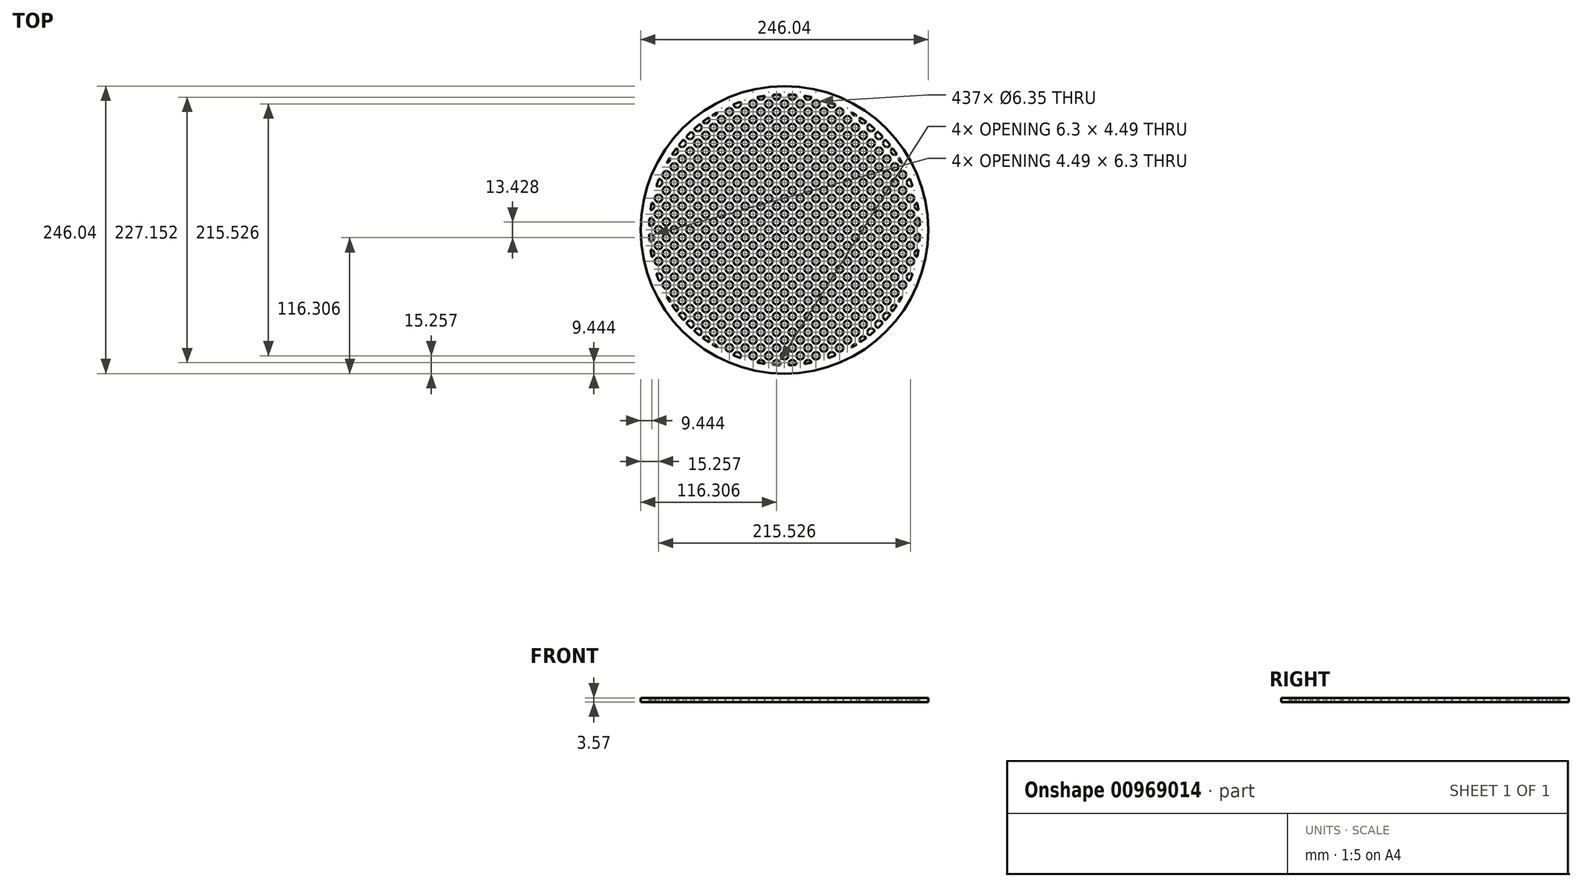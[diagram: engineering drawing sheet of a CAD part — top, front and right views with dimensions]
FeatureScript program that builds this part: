
annotation { "Feature Type Name" : "Feature", "Feature Type Description" : "" }
export const myFeature = defineFeature(function(context is Context, id is Id, definition is map)
    precondition{}
    {
        {
            var Q0;
            Q0=qCreatedBy(makeId("Top.planeOp"),FACE);
            var sketch = newSketch(context, id + "F0", { "sketchPlane" : qUnion([Q0])});
            skCircle(sketch, "E0", {"center": v(0, 0) * mm, "radius": 123.02 * mm});
            skSolve(sketch);
        }
        {
            var Q0;
            Q0 = qSketchRegion(id + "F0", true);
            extrude(context, id + "F1", {"entities" : qUnion([Q0]), "depth" : 3.57 * mm, "offsetDistance" : 25.4 * mm});
        }
        {
            var Q0;
            Q0=makeQuery(id+"F1.opExtrude","CAP_FACE",FACE,{"disambiguationData":[OSD([sQuery(id+"F0.wireOp",EDGE,"E0")])],"isStart":false});
            var sketch = newSketch(context, id + "F2", { "sketchPlane" : qUnion([Q0])});
            skCircle(sketch, "E1", {"center": v(-175.11, -121.23) * mm, "radius": 3.18 * mm});
            skCircle(sketch, "E2", {"center": v(-168.38, -114.5) * mm, "radius": 3.18 * mm});
            skLineSegment(sketch, "E3", {"start": v(-175.04, -116.82) * mm, "end": v(-170.43, -121.43) * mm, "construction": true});
            skLineSegment(sketch, "E4", {"start": v(-173.02, -114.35) * mm, "end": v(-167.94, -119.43) * mm, "construction": true});
            skLineSegment(sketch, "E5", {"start": v(-175.11, -121.23) * mm, "end": v(-168.38, -114.5) * mm, "construction": true});
            skCircle(sketch, "E6.0.1.0", {"center": v(-175.11, -107.76) * mm, "radius": 3.18 * mm});
            skCircle(sketch, "E6.0.2.0", {"center": v(-175.11, -94.3) * mm, "radius": 3.18 * mm});
            skCircle(sketch, "E6.1.0.0", {"center": v(-161.64, -121.23) * mm, "radius": 3.18 * mm});
            skCircle(sketch, "E6.1.1.0", {"center": v(-161.64, -107.76) * mm, "radius": 3.18 * mm});
            skCircle(sketch, "E6.1.2.0", {"center": v(-161.64, -94.3) * mm, "radius": 3.18 * mm});
            skCircle(sketch, "E6.2.0.0", {"center": v(-148.17, -121.23) * mm, "radius": 3.18 * mm});
            skCircle(sketch, "E6.2.1.0", {"center": v(-148.17, -107.76) * mm, "radius": 3.18 * mm});
            skCircle(sketch, "E6.2.2.0", {"center": v(-148.17, -94.3) * mm, "radius": 3.18 * mm});
            skLineSegment(sketch, "E6.direction1", {"start": v(-175.11, -121.23) * mm, "end": v(-161.64, -121.23) * mm, "construction": true});
            skLineSegment(sketch, "E6.direction2", {"start": v(-175.11, -121.23) * mm, "end": v(-175.11, -107.76) * mm, "construction": true});
            skCircle(sketch, "E7.0.1.0", {"center": v(-168.38, -101.03) * mm, "radius": 3.18 * mm});
            skCircle(sketch, "E7.0.2.0", {"center": v(-168.38, -87.56) * mm, "radius": 3.18 * mm});
            skCircle(sketch, "E7.1.0.0", {"center": v(-154.9, -114.5) * mm, "radius": 3.18 * mm});
            skCircle(sketch, "E7.1.1.0", {"center": v(-154.9, -101.03) * mm, "radius": 3.18 * mm});
            skCircle(sketch, "E7.1.2.0", {"center": v(-154.9, -87.56) * mm, "radius": 3.18 * mm});
            skCircle(sketch, "E7.2.0.0", {"center": v(-141.44, -114.5) * mm, "radius": 3.18 * mm});
            skCircle(sketch, "E7.2.1.0", {"center": v(-141.44, -101.03) * mm, "radius": 3.18 * mm});
            skCircle(sketch, "E7.2.2.0", {"center": v(-141.44, -87.56) * mm, "radius": 3.18 * mm});
            skLineSegment(sketch, "E7.direction1", {"start": v(-168.38, -114.5) * mm, "end": v(-154.9, -114.5) * mm, "construction": true});
            skLineSegment(sketch, "E7.direction2", {"start": v(-168.38, -114.5) * mm, "end": v(-168.38, -101.03) * mm, "construction": true});
            skCircle(sketch, "E8.0.0.3", {"center": v(-168.38, -74.09) * mm, "radius": 3.18 * mm});
            skCircle(sketch, "E8.0.0.4", {"center": v(-168.38, -60.62) * mm, "radius": 3.18 * mm});
            skCircle(sketch, "E8.0.0.5", {"center": v(-168.38, -47.15) * mm, "radius": 3.18 * mm});
            skCircle(sketch, "E8.0.0.6", {"center": v(-168.38, -33.68) * mm, "radius": 3.18 * mm});
            skCircle(sketch, "E8.0.0.7", {"center": v(-168.38, -20.2) * mm, "radius": 3.18 * mm});
            skCircle(sketch, "E8.0.0.8", {"center": v(-168.38, -6.74) * mm, "radius": 3.18 * mm});
            skCircle(sketch, "E8.0.0.9", {"center": v(-168.38, 6.74) * mm, "radius": 3.18 * mm});
            skCircle(sketch, "E8.0.0.10", {"center": v(-168.38, 20.2) * mm, "radius": 3.18 * mm});
            skCircle(sketch, "E8.0.0.11", {"center": v(-168.38, 33.68) * mm, "radius": 3.18 * mm});
            skCircle(sketch, "E8.0.0.12", {"center": v(-168.38, 47.15) * mm, "radius": 3.18 * mm});
            skCircle(sketch, "E8.0.0.13", {"center": v(-168.38, 60.62) * mm, "radius": 3.18 * mm});
            skCircle(sketch, "E8.0.0.14", {"center": v(-168.38, 74.09) * mm, "radius": 3.18 * mm});
            skCircle(sketch, "E8.0.0.15", {"center": v(-168.38, 87.56) * mm, "radius": 3.18 * mm});
            skCircle(sketch, "E8.0.0.16", {"center": v(-168.38, 101.03) * mm, "radius": 3.18 * mm});
            skCircle(sketch, "E8.0.0.17", {"center": v(-168.38, 114.5) * mm, "radius": 3.18 * mm});
            skCircle(sketch, "E8.0.0.18", {"center": v(-168.38, 127.97) * mm, "radius": 3.18 * mm});
            skCircle(sketch, "E8.0.0.19", {"center": v(-168.38, 141.44) * mm, "radius": 3.18 * mm});
            skCircle(sketch, "E8.0.0.20", {"center": v(-168.38, 154.9) * mm, "radius": 3.18 * mm});
            skCircle(sketch, "E8.0.0.21", {"center": v(-168.38, 168.38) * mm, "radius": 3.18 * mm});
            skCircle(sketch, "E8.0.0.22", {"center": v(-168.38, 181.85) * mm, "radius": 3.18 * mm});
            skCircle(sketch, "E8.0.0.23", {"center": v(-168.38, 195.32) * mm, "radius": 3.18 * mm});
            skCircle(sketch, "E8.0.0.24", {"center": v(-168.38, 208.8) * mm, "radius": 3.18 * mm});
            skCircle(sketch, "E8.0.1.3", {"center": v(-154.9, -74.09) * mm, "radius": 3.18 * mm});
            skCircle(sketch, "E8.0.1.4", {"center": v(-154.9, -60.62) * mm, "radius": 3.18 * mm});
            skCircle(sketch, "E8.0.1.5", {"center": v(-154.9, -47.15) * mm, "radius": 3.18 * mm});
            skCircle(sketch, "E8.0.1.6", {"center": v(-154.9, -33.68) * mm, "radius": 3.18 * mm});
            skCircle(sketch, "E8.0.1.7", {"center": v(-154.9, -20.2) * mm, "radius": 3.18 * mm});
            skCircle(sketch, "E8.0.1.8", {"center": v(-154.9, -6.74) * mm, "radius": 3.18 * mm});
            skCircle(sketch, "E8.0.1.9", {"center": v(-154.9, 6.74) * mm, "radius": 3.18 * mm});
            skCircle(sketch, "E8.0.1.10", {"center": v(-154.9, 20.2) * mm, "radius": 3.18 * mm});
            skCircle(sketch, "E8.0.1.11", {"center": v(-154.9, 33.68) * mm, "radius": 3.18 * mm});
            skCircle(sketch, "E8.0.1.12", {"center": v(-154.9, 47.15) * mm, "radius": 3.18 * mm});
            skCircle(sketch, "E8.0.1.13", {"center": v(-154.9, 60.62) * mm, "radius": 3.18 * mm});
            skCircle(sketch, "E8.0.1.14", {"center": v(-154.9, 74.09) * mm, "radius": 3.18 * mm});
            skCircle(sketch, "E8.0.1.15", {"center": v(-154.9, 87.56) * mm, "radius": 3.18 * mm});
            skCircle(sketch, "E8.0.1.16", {"center": v(-154.9, 101.03) * mm, "radius": 3.18 * mm});
            skCircle(sketch, "E8.0.1.17", {"center": v(-154.9, 114.5) * mm, "radius": 3.18 * mm});
            skCircle(sketch, "E8.0.1.18", {"center": v(-154.9, 127.97) * mm, "radius": 3.18 * mm});
            skCircle(sketch, "E8.0.1.19", {"center": v(-154.9, 141.44) * mm, "radius": 3.18 * mm});
            skCircle(sketch, "E8.0.1.20", {"center": v(-154.9, 154.9) * mm, "radius": 3.18 * mm});
            skCircle(sketch, "E8.0.1.21", {"center": v(-154.9, 168.38) * mm, "radius": 3.18 * mm});
            skCircle(sketch, "E8.0.1.22", {"center": v(-154.9, 181.85) * mm, "radius": 3.18 * mm});
            skCircle(sketch, "E8.0.1.23", {"center": v(-154.9, 195.32) * mm, "radius": 3.18 * mm});
            skCircle(sketch, "E8.0.1.24", {"center": v(-154.9, 208.8) * mm, "radius": 3.18 * mm});
            skCircle(sketch, "E8.0.2.3", {"center": v(-141.44, -74.09) * mm, "radius": 3.18 * mm});
            skCircle(sketch, "E8.0.2.4", {"center": v(-141.44, -60.62) * mm, "radius": 3.18 * mm});
            skCircle(sketch, "E8.0.2.5", {"center": v(-141.44, -47.15) * mm, "radius": 3.18 * mm});
            skCircle(sketch, "E8.0.2.6", {"center": v(-141.44, -33.68) * mm, "radius": 3.18 * mm});
            skCircle(sketch, "E8.0.2.7", {"center": v(-141.44, -20.2) * mm, "radius": 3.18 * mm});
            skCircle(sketch, "E8.0.2.8", {"center": v(-141.44, -6.74) * mm, "radius": 3.18 * mm});
            skCircle(sketch, "E8.0.2.9", {"center": v(-141.44, 6.74) * mm, "radius": 3.18 * mm});
            skCircle(sketch, "E8.0.2.10", {"center": v(-141.44, 20.2) * mm, "radius": 3.18 * mm});
            skCircle(sketch, "E8.0.2.11", {"center": v(-141.44, 33.68) * mm, "radius": 3.18 * mm});
            skCircle(sketch, "E8.0.2.12", {"center": v(-141.44, 47.15) * mm, "radius": 3.18 * mm});
            skCircle(sketch, "E8.0.2.13", {"center": v(-141.44, 60.62) * mm, "radius": 3.18 * mm});
            skCircle(sketch, "E8.0.2.14", {"center": v(-141.44, 74.09) * mm, "radius": 3.18 * mm});
            skCircle(sketch, "E8.0.2.15", {"center": v(-141.44, 87.56) * mm, "radius": 3.18 * mm});
            skCircle(sketch, "E8.0.2.16", {"center": v(-141.44, 101.03) * mm, "radius": 3.18 * mm});
            skCircle(sketch, "E8.0.2.17", {"center": v(-141.44, 114.5) * mm, "radius": 3.18 * mm});
            skCircle(sketch, "E8.0.2.18", {"center": v(-141.44, 127.97) * mm, "radius": 3.18 * mm});
            skCircle(sketch, "E8.0.2.19", {"center": v(-141.44, 141.44) * mm, "radius": 3.18 * mm});
            skCircle(sketch, "E8.0.2.20", {"center": v(-141.44, 154.9) * mm, "radius": 3.18 * mm});
            skCircle(sketch, "E8.0.2.21", {"center": v(-141.44, 168.38) * mm, "radius": 3.18 * mm});
            skCircle(sketch, "E8.0.2.22", {"center": v(-141.44, 181.85) * mm, "radius": 3.18 * mm});
            skCircle(sketch, "E8.0.2.23", {"center": v(-141.44, 195.32) * mm, "radius": 3.18 * mm});
            skCircle(sketch, "E8.0.2.24", {"center": v(-141.44, 208.8) * mm, "radius": 3.18 * mm});
            skCircle(sketch, "E9.0.0.3", {"center": v(-175.11, -80.82) * mm, "radius": 3.18 * mm});
            skCircle(sketch, "E9.0.0.4", {"center": v(-175.11, -67.35) * mm, "radius": 3.18 * mm});
            skCircle(sketch, "E9.0.0.5", {"center": v(-175.11, -53.88) * mm, "radius": 3.18 * mm});
            skCircle(sketch, "E9.0.0.6", {"center": v(-175.11, -40.41) * mm, "radius": 3.18 * mm});
            skCircle(sketch, "E9.0.0.7", {"center": v(-175.11, -26.94) * mm, "radius": 3.18 * mm});
            skCircle(sketch, "E9.0.0.8", {"center": v(-175.11, -13.47) * mm, "radius": 3.18 * mm});
            skCircle(sketch, "E9.0.0.9", {"center": v(-175.11, 0) * mm, "radius": 3.18 * mm});
            skCircle(sketch, "E9.0.0.10", {"center": v(-175.11, 13.47) * mm, "radius": 3.18 * mm});
            skCircle(sketch, "E9.0.0.11", {"center": v(-175.11, 26.94) * mm, "radius": 3.18 * mm});
            skCircle(sketch, "E9.0.0.12", {"center": v(-175.11, 40.41) * mm, "radius": 3.18 * mm});
            skCircle(sketch, "E9.0.0.13", {"center": v(-175.11, 53.88) * mm, "radius": 3.18 * mm});
            skCircle(sketch, "E9.0.0.14", {"center": v(-175.11, 67.35) * mm, "radius": 3.18 * mm});
            skCircle(sketch, "E9.0.0.15", {"center": v(-175.11, 80.82) * mm, "radius": 3.18 * mm});
            skCircle(sketch, "E9.0.0.16", {"center": v(-175.11, 94.3) * mm, "radius": 3.18 * mm});
            skCircle(sketch, "E9.0.0.17", {"center": v(-175.11, 107.76) * mm, "radius": 3.18 * mm});
            skCircle(sketch, "E9.0.0.18", {"center": v(-175.11, 121.23) * mm, "radius": 3.18 * mm});
            skCircle(sketch, "E9.0.0.19", {"center": v(-175.11, 134.7) * mm, "radius": 3.18 * mm});
            skCircle(sketch, "E9.0.0.20", {"center": v(-175.11, 148.17) * mm, "radius": 3.18 * mm});
            skCircle(sketch, "E9.0.0.21", {"center": v(-175.11, 161.64) * mm, "radius": 3.18 * mm});
            skCircle(sketch, "E9.0.0.22", {"center": v(-175.11, 175.11) * mm, "radius": 3.18 * mm});
            skCircle(sketch, "E9.0.0.23", {"center": v(-175.11, 188.59) * mm, "radius": 3.18 * mm});
            skCircle(sketch, "E9.0.0.24", {"center": v(-175.11, 202.06) * mm, "radius": 3.18 * mm});
            skCircle(sketch, "E9.0.1.3", {"center": v(-161.64, -80.82) * mm, "radius": 3.18 * mm});
            skCircle(sketch, "E9.0.1.4", {"center": v(-161.64, -67.35) * mm, "radius": 3.18 * mm});
            skCircle(sketch, "E9.0.1.5", {"center": v(-161.64, -53.88) * mm, "radius": 3.18 * mm});
            skCircle(sketch, "E9.0.1.6", {"center": v(-161.64, -40.41) * mm, "radius": 3.18 * mm});
            skCircle(sketch, "E9.0.1.7", {"center": v(-161.64, -26.94) * mm, "radius": 3.18 * mm});
            skCircle(sketch, "E9.0.1.8", {"center": v(-161.64, -13.47) * mm, "radius": 3.18 * mm});
            skCircle(sketch, "E9.0.1.9", {"center": v(-161.64, 0) * mm, "radius": 3.18 * mm});
            skCircle(sketch, "E9.0.1.10", {"center": v(-161.64, 13.47) * mm, "radius": 3.18 * mm});
            skCircle(sketch, "E9.0.1.11", {"center": v(-161.64, 26.94) * mm, "radius": 3.18 * mm});
            skCircle(sketch, "E9.0.1.12", {"center": v(-161.64, 40.41) * mm, "radius": 3.18 * mm});
            skCircle(sketch, "E9.0.1.13", {"center": v(-161.64, 53.88) * mm, "radius": 3.18 * mm});
            skCircle(sketch, "E9.0.1.14", {"center": v(-161.64, 67.35) * mm, "radius": 3.18 * mm});
            skCircle(sketch, "E9.0.1.15", {"center": v(-161.64, 80.82) * mm, "radius": 3.18 * mm});
            skCircle(sketch, "E9.0.1.16", {"center": v(-161.64, 94.3) * mm, "radius": 3.18 * mm});
            skCircle(sketch, "E9.0.1.17", {"center": v(-161.64, 107.76) * mm, "radius": 3.18 * mm});
            skCircle(sketch, "E9.0.1.18", {"center": v(-161.64, 121.23) * mm, "radius": 3.18 * mm});
            skCircle(sketch, "E9.0.1.19", {"center": v(-161.64, 134.7) * mm, "radius": 3.18 * mm});
            skCircle(sketch, "E9.0.1.20", {"center": v(-161.64, 148.17) * mm, "radius": 3.18 * mm});
            skCircle(sketch, "E9.0.1.21", {"center": v(-161.64, 161.64) * mm, "radius": 3.18 * mm});
            skCircle(sketch, "E9.0.1.22", {"center": v(-161.64, 175.11) * mm, "radius": 3.18 * mm});
            skCircle(sketch, "E9.0.1.23", {"center": v(-161.64, 188.59) * mm, "radius": 3.18 * mm});
            skCircle(sketch, "E9.0.1.24", {"center": v(-161.64, 202.06) * mm, "radius": 3.18 * mm});
            skCircle(sketch, "E9.0.2.3", {"center": v(-148.17, -80.82) * mm, "radius": 3.18 * mm});
            skCircle(sketch, "E9.0.2.4", {"center": v(-148.17, -67.35) * mm, "radius": 3.18 * mm});
            skCircle(sketch, "E9.0.2.5", {"center": v(-148.17, -53.88) * mm, "radius": 3.18 * mm});
            skCircle(sketch, "E9.0.2.6", {"center": v(-148.17, -40.41) * mm, "radius": 3.18 * mm});
            skCircle(sketch, "E9.0.2.7", {"center": v(-148.17, -26.94) * mm, "radius": 3.18 * mm});
            skCircle(sketch, "E9.0.2.8", {"center": v(-148.17, -13.47) * mm, "radius": 3.18 * mm});
            skCircle(sketch, "E9.0.2.9", {"center": v(-148.17, 0) * mm, "radius": 3.18 * mm});
            skCircle(sketch, "E9.0.2.10", {"center": v(-148.17, 13.47) * mm, "radius": 3.18 * mm});
            skCircle(sketch, "E9.0.2.11", {"center": v(-148.17, 26.94) * mm, "radius": 3.18 * mm});
            skCircle(sketch, "E9.0.2.12", {"center": v(-148.17, 40.41) * mm, "radius": 3.18 * mm});
            skCircle(sketch, "E9.0.2.13", {"center": v(-148.17, 53.88) * mm, "radius": 3.18 * mm});
            skCircle(sketch, "E9.0.2.14", {"center": v(-148.17, 67.35) * mm, "radius": 3.18 * mm});
            skCircle(sketch, "E9.0.2.15", {"center": v(-148.17, 80.82) * mm, "radius": 3.18 * mm});
            skCircle(sketch, "E9.0.2.16", {"center": v(-148.17, 94.3) * mm, "radius": 3.18 * mm});
            skCircle(sketch, "E9.0.2.17", {"center": v(-148.17, 107.76) * mm, "radius": 3.18 * mm});
            skCircle(sketch, "E9.0.2.18", {"center": v(-148.17, 121.23) * mm, "radius": 3.18 * mm});
            skCircle(sketch, "E9.0.2.19", {"center": v(-148.17, 134.7) * mm, "radius": 3.18 * mm});
            skCircle(sketch, "E9.0.2.20", {"center": v(-148.17, 148.17) * mm, "radius": 3.18 * mm});
            skCircle(sketch, "E9.0.2.21", {"center": v(-148.17, 161.64) * mm, "radius": 3.18 * mm});
            skCircle(sketch, "E9.0.2.22", {"center": v(-148.17, 175.11) * mm, "radius": 3.18 * mm});
            skCircle(sketch, "E9.0.2.23", {"center": v(-148.17, 188.59) * mm, "radius": 3.18 * mm});
            skCircle(sketch, "E9.0.2.24", {"center": v(-148.17, 202.06) * mm, "radius": 3.18 * mm});
            skCircle(sketch, "E10.0.3.0", {"center": v(-134.7, -121.23) * mm, "radius": 3.18 * mm});
            skCircle(sketch, "E10.0.3.1", {"center": v(-134.7, -107.76) * mm, "radius": 3.18 * mm});
            skCircle(sketch, "E10.0.3.2", {"center": v(-134.7, -94.3) * mm, "radius": 3.18 * mm});
            skCircle(sketch, "E10.0.3.3", {"center": v(-134.7, -80.82) * mm, "radius": 3.18 * mm});
            skCircle(sketch, "E10.0.3.4", {"center": v(-134.7, -67.35) * mm, "radius": 3.18 * mm});
            skCircle(sketch, "E10.0.3.5", {"center": v(-134.7, -53.88) * mm, "radius": 3.18 * mm});
            skCircle(sketch, "E10.0.3.6", {"center": v(-134.7, -40.41) * mm, "radius": 3.18 * mm});
            skCircle(sketch, "E10.0.3.7", {"center": v(-134.7, -26.94) * mm, "radius": 3.18 * mm});
            skCircle(sketch, "E10.0.3.8", {"center": v(-134.7, -13.47) * mm, "radius": 3.18 * mm});
            skCircle(sketch, "E10.0.3.9", {"center": v(-134.7, 0) * mm, "radius": 3.18 * mm});
            skCircle(sketch, "E10.0.3.10", {"center": v(-134.7, 13.47) * mm, "radius": 3.18 * mm});
            skCircle(sketch, "E10.0.3.11", {"center": v(-134.7, 26.94) * mm, "radius": 3.18 * mm});
            skCircle(sketch, "E10.0.3.12", {"center": v(-134.7, 40.41) * mm, "radius": 3.18 * mm});
            skCircle(sketch, "E10.0.3.13", {"center": v(-134.7, 53.88) * mm, "radius": 3.18 * mm});
            skCircle(sketch, "E10.0.3.14", {"center": v(-134.7, 67.35) * mm, "radius": 3.18 * mm});
            skCircle(sketch, "E10.0.3.15", {"center": v(-134.7, 80.82) * mm, "radius": 3.18 * mm});
            skCircle(sketch, "E10.0.3.16", {"center": v(-134.7, 94.3) * mm, "radius": 3.18 * mm});
            skCircle(sketch, "E10.0.3.17", {"center": v(-134.7, 107.76) * mm, "radius": 3.18 * mm});
            skCircle(sketch, "E10.0.3.18", {"center": v(-134.7, 121.23) * mm, "radius": 3.18 * mm});
            skCircle(sketch, "E10.0.3.19", {"center": v(-134.7, 134.7) * mm, "radius": 3.18 * mm});
            skCircle(sketch, "E10.0.3.20", {"center": v(-134.7, 148.17) * mm, "radius": 3.18 * mm});
            skCircle(sketch, "E10.0.3.21", {"center": v(-134.7, 161.64) * mm, "radius": 3.18 * mm});
            skCircle(sketch, "E10.0.3.22", {"center": v(-134.7, 175.11) * mm, "radius": 3.18 * mm});
            skCircle(sketch, "E10.0.3.23", {"center": v(-134.7, 188.59) * mm, "radius": 3.18 * mm});
            skCircle(sketch, "E10.0.3.24", {"center": v(-134.7, 202.06) * mm, "radius": 3.18 * mm});
            skCircle(sketch, "E10.0.4.0", {"center": v(-121.23, -121.23) * mm, "radius": 3.18 * mm});
            skCircle(sketch, "E10.0.4.1", {"center": v(-121.23, -107.76) * mm, "radius": 3.18 * mm});
            skCircle(sketch, "E10.0.4.2", {"center": v(-121.23, -94.3) * mm, "radius": 3.18 * mm});
            skCircle(sketch, "E10.0.4.3", {"center": v(-121.23, -80.82) * mm, "radius": 3.18 * mm});
            skCircle(sketch, "E10.0.4.4", {"center": v(-121.23, -67.35) * mm, "radius": 3.18 * mm});
            skCircle(sketch, "E10.0.4.5", {"center": v(-121.23, -53.88) * mm, "radius": 3.18 * mm});
            skCircle(sketch, "E10.0.4.6", {"center": v(-121.23, -40.41) * mm, "radius": 3.18 * mm});
            skCircle(sketch, "E10.0.4.7", {"center": v(-121.23, -26.94) * mm, "radius": 3.18 * mm});
            skCircle(sketch, "E10.0.4.8", {"center": v(-121.23, -13.47) * mm, "radius": 3.18 * mm});
            skCircle(sketch, "E10.0.4.9", {"center": v(-121.23, 0) * mm, "radius": 3.18 * mm});
            skCircle(sketch, "E10.0.4.10", {"center": v(-121.23, 13.47) * mm, "radius": 3.18 * mm});
            skCircle(sketch, "E10.0.4.11", {"center": v(-121.23, 26.94) * mm, "radius": 3.18 * mm});
            skCircle(sketch, "E10.0.4.12", {"center": v(-121.23, 40.41) * mm, "radius": 3.18 * mm});
            skCircle(sketch, "E10.0.4.13", {"center": v(-121.23, 53.88) * mm, "radius": 3.18 * mm});
            skCircle(sketch, "E10.0.4.14", {"center": v(-121.23, 67.35) * mm, "radius": 3.18 * mm});
            skCircle(sketch, "E10.0.4.15", {"center": v(-121.23, 80.82) * mm, "radius": 3.18 * mm});
            skCircle(sketch, "E10.0.4.16", {"center": v(-121.23, 94.3) * mm, "radius": 3.18 * mm});
            skCircle(sketch, "E10.0.4.17", {"center": v(-121.23, 107.76) * mm, "radius": 3.18 * mm});
            skCircle(sketch, "E10.0.4.18", {"center": v(-121.23, 121.23) * mm, "radius": 3.18 * mm});
            skCircle(sketch, "E10.0.4.19", {"center": v(-121.23, 134.7) * mm, "radius": 3.18 * mm});
            skCircle(sketch, "E10.0.4.20", {"center": v(-121.23, 148.17) * mm, "radius": 3.18 * mm});
            skCircle(sketch, "E10.0.4.21", {"center": v(-121.23, 161.64) * mm, "radius": 3.18 * mm});
            skCircle(sketch, "E10.0.4.22", {"center": v(-121.23, 175.11) * mm, "radius": 3.18 * mm});
            skCircle(sketch, "E10.0.4.23", {"center": v(-121.23, 188.59) * mm, "radius": 3.18 * mm});
            skCircle(sketch, "E10.0.4.24", {"center": v(-121.23, 202.06) * mm, "radius": 3.18 * mm});
            skCircle(sketch, "E10.0.5.0", {"center": v(-107.76, -121.23) * mm, "radius": 3.18 * mm});
            skCircle(sketch, "E10.0.5.1", {"center": v(-107.76, -107.76) * mm, "radius": 3.18 * mm});
            skCircle(sketch, "E10.0.5.2", {"center": v(-107.76, -94.3) * mm, "radius": 3.18 * mm});
            skCircle(sketch, "E10.0.5.3", {"center": v(-107.76, -80.82) * mm, "radius": 3.18 * mm});
            skCircle(sketch, "E10.0.5.4", {"center": v(-107.76, -67.35) * mm, "radius": 3.18 * mm});
            skCircle(sketch, "E10.0.5.5", {"center": v(-107.76, -53.88) * mm, "radius": 3.18 * mm});
            skCircle(sketch, "E10.0.5.6", {"center": v(-107.76, -40.41) * mm, "radius": 3.18 * mm});
            skCircle(sketch, "E10.0.5.7", {"center": v(-107.76, -26.94) * mm, "radius": 3.18 * mm});
            skCircle(sketch, "E10.0.5.8", {"center": v(-107.76, -13.47) * mm, "radius": 3.18 * mm});
            skCircle(sketch, "E10.0.5.9", {"center": v(-107.76, 0) * mm, "radius": 3.18 * mm});
            skCircle(sketch, "E10.0.5.10", {"center": v(-107.76, 13.47) * mm, "radius": 3.18 * mm});
            skCircle(sketch, "E10.0.5.11", {"center": v(-107.76, 26.94) * mm, "radius": 3.18 * mm});
            skCircle(sketch, "E10.0.5.12", {"center": v(-107.76, 40.41) * mm, "radius": 3.18 * mm});
            skCircle(sketch, "E10.0.5.13", {"center": v(-107.76, 53.88) * mm, "radius": 3.18 * mm});
            skCircle(sketch, "E10.0.5.14", {"center": v(-107.76, 67.35) * mm, "radius": 3.18 * mm});
            skCircle(sketch, "E10.0.5.15", {"center": v(-107.76, 80.82) * mm, "radius": 3.18 * mm});
            skCircle(sketch, "E10.0.5.16", {"center": v(-107.76, 94.3) * mm, "radius": 3.18 * mm});
            skCircle(sketch, "E10.0.5.17", {"center": v(-107.76, 107.76) * mm, "radius": 3.18 * mm});
            skCircle(sketch, "E10.0.5.18", {"center": v(-107.76, 121.23) * mm, "radius": 3.18 * mm});
            skCircle(sketch, "E10.0.5.19", {"center": v(-107.76, 134.7) * mm, "radius": 3.18 * mm});
            skCircle(sketch, "E10.0.5.20", {"center": v(-107.76, 148.17) * mm, "radius": 3.18 * mm});
            skCircle(sketch, "E10.0.5.21", {"center": v(-107.76, 161.64) * mm, "radius": 3.18 * mm});
            skCircle(sketch, "E10.0.5.22", {"center": v(-107.76, 175.11) * mm, "radius": 3.18 * mm});
            skCircle(sketch, "E10.0.5.23", {"center": v(-107.76, 188.59) * mm, "radius": 3.18 * mm});
            skCircle(sketch, "E10.0.5.24", {"center": v(-107.76, 202.06) * mm, "radius": 3.18 * mm});
            skCircle(sketch, "E10.0.6.0", {"center": v(-94.3, -121.23) * mm, "radius": 3.18 * mm});
            skCircle(sketch, "E10.0.6.1", {"center": v(-94.3, -107.76) * mm, "radius": 3.18 * mm});
            skCircle(sketch, "E10.0.6.2", {"center": v(-94.3, -94.3) * mm, "radius": 3.18 * mm});
            skCircle(sketch, "E10.0.6.3", {"center": v(-94.3, -80.82) * mm, "radius": 3.18 * mm});
            skCircle(sketch, "E10.0.6.4", {"center": v(-94.3, -67.35) * mm, "radius": 3.18 * mm});
            skCircle(sketch, "E10.0.6.5", {"center": v(-94.3, -53.88) * mm, "radius": 3.18 * mm});
            skCircle(sketch, "E10.0.6.6", {"center": v(-94.3, -40.41) * mm, "radius": 3.18 * mm});
            skCircle(sketch, "E10.0.6.7", {"center": v(-94.3, -26.94) * mm, "radius": 3.18 * mm});
            skCircle(sketch, "E10.0.6.8", {"center": v(-94.3, -13.47) * mm, "radius": 3.18 * mm});
            skCircle(sketch, "E10.0.6.9", {"center": v(-94.3, 0) * mm, "radius": 3.18 * mm});
            skCircle(sketch, "E10.0.6.10", {"center": v(-94.3, 13.47) * mm, "radius": 3.18 * mm});
            skCircle(sketch, "E10.0.6.11", {"center": v(-94.3, 26.94) * mm, "radius": 3.18 * mm});
            skCircle(sketch, "E10.0.6.12", {"center": v(-94.3, 40.41) * mm, "radius": 3.18 * mm});
            skCircle(sketch, "E10.0.6.13", {"center": v(-94.3, 53.88) * mm, "radius": 3.18 * mm});
            skCircle(sketch, "E10.0.6.14", {"center": v(-94.3, 67.35) * mm, "radius": 3.18 * mm});
            skCircle(sketch, "E10.0.6.15", {"center": v(-94.3, 80.82) * mm, "radius": 3.18 * mm});
            skCircle(sketch, "E10.0.6.16", {"center": v(-94.3, 94.3) * mm, "radius": 3.18 * mm});
            skCircle(sketch, "E10.0.6.17", {"center": v(-94.3, 107.76) * mm, "radius": 3.18 * mm});
            skCircle(sketch, "E10.0.6.18", {"center": v(-94.3, 121.23) * mm, "radius": 3.18 * mm});
            skCircle(sketch, "E10.0.6.19", {"center": v(-94.3, 134.7) * mm, "radius": 3.18 * mm});
            skCircle(sketch, "E10.0.6.20", {"center": v(-94.3, 148.17) * mm, "radius": 3.18 * mm});
            skCircle(sketch, "E10.0.6.21", {"center": v(-94.3, 161.64) * mm, "radius": 3.18 * mm});
            skCircle(sketch, "E10.0.6.22", {"center": v(-94.3, 175.11) * mm, "radius": 3.18 * mm});
            skCircle(sketch, "E10.0.6.23", {"center": v(-94.3, 188.59) * mm, "radius": 3.18 * mm});
            skCircle(sketch, "E10.0.6.24", {"center": v(-94.3, 202.06) * mm, "radius": 3.18 * mm});
            skCircle(sketch, "E10.0.7.0", {"center": v(-80.82, -121.23) * mm, "radius": 3.18 * mm});
            skCircle(sketch, "E10.0.7.1", {"center": v(-80.82, -107.76) * mm, "radius": 3.18 * mm});
            skCircle(sketch, "E10.0.7.2", {"center": v(-80.82, -94.3) * mm, "radius": 3.18 * mm});
            skCircle(sketch, "E10.0.7.3", {"center": v(-80.82, -80.82) * mm, "radius": 3.18 * mm});
            skCircle(sketch, "E10.0.7.4", {"center": v(-80.82, -67.35) * mm, "radius": 3.18 * mm});
            skCircle(sketch, "E10.0.7.5", {"center": v(-80.82, -53.88) * mm, "radius": 3.18 * mm});
            skCircle(sketch, "E10.0.7.6", {"center": v(-80.82, -40.41) * mm, "radius": 3.18 * mm});
            skCircle(sketch, "E10.0.7.7", {"center": v(-80.82, -26.94) * mm, "radius": 3.18 * mm});
            skCircle(sketch, "E10.0.7.8", {"center": v(-80.82, -13.47) * mm, "radius": 3.18 * mm});
            skCircle(sketch, "E10.0.7.9", {"center": v(-80.82, 0) * mm, "radius": 3.18 * mm});
            skCircle(sketch, "E10.0.7.10", {"center": v(-80.82, 13.47) * mm, "radius": 3.18 * mm});
            skCircle(sketch, "E10.0.7.11", {"center": v(-80.82, 26.94) * mm, "radius": 3.18 * mm});
            skCircle(sketch, "E10.0.7.12", {"center": v(-80.82, 40.41) * mm, "radius": 3.18 * mm});
            skCircle(sketch, "E10.0.7.13", {"center": v(-80.82, 53.88) * mm, "radius": 3.18 * mm});
            skCircle(sketch, "E10.0.7.14", {"center": v(-80.82, 67.35) * mm, "radius": 3.18 * mm});
            skCircle(sketch, "E10.0.7.15", {"center": v(-80.82, 80.82) * mm, "radius": 3.18 * mm});
            skCircle(sketch, "E10.0.7.16", {"center": v(-80.82, 94.3) * mm, "radius": 3.18 * mm});
            skCircle(sketch, "E10.0.7.17", {"center": v(-80.82, 107.76) * mm, "radius": 3.18 * mm});
            skCircle(sketch, "E10.0.7.18", {"center": v(-80.82, 121.23) * mm, "radius": 3.18 * mm});
            skCircle(sketch, "E10.0.7.19", {"center": v(-80.82, 134.7) * mm, "radius": 3.18 * mm});
            skCircle(sketch, "E10.0.7.20", {"center": v(-80.82, 148.17) * mm, "radius": 3.18 * mm});
            skCircle(sketch, "E10.0.7.21", {"center": v(-80.82, 161.64) * mm, "radius": 3.18 * mm});
            skCircle(sketch, "E10.0.7.22", {"center": v(-80.82, 175.11) * mm, "radius": 3.18 * mm});
            skCircle(sketch, "E10.0.7.23", {"center": v(-80.82, 188.59) * mm, "radius": 3.18 * mm});
            skCircle(sketch, "E10.0.7.24", {"center": v(-80.82, 202.06) * mm, "radius": 3.18 * mm});
            skCircle(sketch, "E10.0.8.0", {"center": v(-67.35, -121.23) * mm, "radius": 3.18 * mm});
            skCircle(sketch, "E10.0.8.1", {"center": v(-67.35, -107.76) * mm, "radius": 3.18 * mm});
            skCircle(sketch, "E10.0.8.2", {"center": v(-67.35, -94.3) * mm, "radius": 3.18 * mm});
            skCircle(sketch, "E10.0.8.3", {"center": v(-67.35, -80.82) * mm, "radius": 3.18 * mm});
            skCircle(sketch, "E10.0.8.4", {"center": v(-67.35, -67.35) * mm, "radius": 3.18 * mm});
            skCircle(sketch, "E10.0.8.5", {"center": v(-67.35, -53.88) * mm, "radius": 3.18 * mm});
            skCircle(sketch, "E10.0.8.6", {"center": v(-67.35, -40.41) * mm, "radius": 3.18 * mm});
            skCircle(sketch, "E10.0.8.7", {"center": v(-67.35, -26.94) * mm, "radius": 3.18 * mm});
            skCircle(sketch, "E10.0.8.8", {"center": v(-67.35, -13.47) * mm, "radius": 3.18 * mm});
            skCircle(sketch, "E10.0.8.9", {"center": v(-67.35, 0) * mm, "radius": 3.18 * mm});
            skCircle(sketch, "E10.0.8.10", {"center": v(-67.35, 13.47) * mm, "radius": 3.18 * mm});
            skCircle(sketch, "E10.0.8.11", {"center": v(-67.35, 26.94) * mm, "radius": 3.18 * mm});
            skCircle(sketch, "E10.0.8.12", {"center": v(-67.35, 40.41) * mm, "radius": 3.18 * mm});
            skCircle(sketch, "E10.0.8.13", {"center": v(-67.35, 53.88) * mm, "radius": 3.18 * mm});
            skCircle(sketch, "E10.0.8.14", {"center": v(-67.35, 67.35) * mm, "radius": 3.18 * mm});
            skCircle(sketch, "E10.0.8.15", {"center": v(-67.35, 80.82) * mm, "radius": 3.18 * mm});
            skCircle(sketch, "E10.0.8.16", {"center": v(-67.35, 94.3) * mm, "radius": 3.18 * mm});
            skCircle(sketch, "E10.0.8.17", {"center": v(-67.35, 107.76) * mm, "radius": 3.18 * mm});
            skCircle(sketch, "E10.0.8.18", {"center": v(-67.35, 121.23) * mm, "radius": 3.18 * mm});
            skCircle(sketch, "E10.0.8.19", {"center": v(-67.35, 134.7) * mm, "radius": 3.18 * mm});
            skCircle(sketch, "E10.0.8.20", {"center": v(-67.35, 148.17) * mm, "radius": 3.18 * mm});
            skCircle(sketch, "E10.0.8.21", {"center": v(-67.35, 161.64) * mm, "radius": 3.18 * mm});
            skCircle(sketch, "E10.0.8.22", {"center": v(-67.35, 175.11) * mm, "radius": 3.18 * mm});
            skCircle(sketch, "E10.0.8.23", {"center": v(-67.35, 188.59) * mm, "radius": 3.18 * mm});
            skCircle(sketch, "E10.0.8.24", {"center": v(-67.35, 202.06) * mm, "radius": 3.18 * mm});
            skCircle(sketch, "E10.0.9.0", {"center": v(-53.88, -121.23) * mm, "radius": 3.18 * mm});
            skCircle(sketch, "E10.0.9.1", {"center": v(-53.88, -107.76) * mm, "radius": 3.18 * mm});
            skCircle(sketch, "E10.0.9.2", {"center": v(-53.88, -94.3) * mm, "radius": 3.18 * mm});
            skCircle(sketch, "E10.0.9.3", {"center": v(-53.88, -80.82) * mm, "radius": 3.18 * mm});
            skCircle(sketch, "E10.0.9.4", {"center": v(-53.88, -67.35) * mm, "radius": 3.18 * mm});
            skCircle(sketch, "E10.0.9.5", {"center": v(-53.88, -53.88) * mm, "radius": 3.18 * mm});
            skCircle(sketch, "E10.0.9.6", {"center": v(-53.88, -40.41) * mm, "radius": 3.18 * mm});
            skCircle(sketch, "E10.0.9.7", {"center": v(-53.88, -26.94) * mm, "radius": 3.18 * mm});
            skCircle(sketch, "E10.0.9.8", {"center": v(-53.88, -13.47) * mm, "radius": 3.18 * mm});
            skCircle(sketch, "E10.0.9.9", {"center": v(-53.88, 0) * mm, "radius": 3.18 * mm});
            skCircle(sketch, "E10.0.9.10", {"center": v(-53.88, 13.47) * mm, "radius": 3.18 * mm});
            skCircle(sketch, "E10.0.9.11", {"center": v(-53.88, 26.94) * mm, "radius": 3.18 * mm});
            skCircle(sketch, "E10.0.9.12", {"center": v(-53.88, 40.41) * mm, "radius": 3.18 * mm});
            skCircle(sketch, "E10.0.9.13", {"center": v(-53.88, 53.88) * mm, "radius": 3.18 * mm});
            skCircle(sketch, "E10.0.9.14", {"center": v(-53.88, 67.35) * mm, "radius": 3.18 * mm});
            skCircle(sketch, "E10.0.9.15", {"center": v(-53.88, 80.82) * mm, "radius": 3.18 * mm});
            skCircle(sketch, "E10.0.9.16", {"center": v(-53.88, 94.3) * mm, "radius": 3.18 * mm});
            skCircle(sketch, "E10.0.9.17", {"center": v(-53.88, 107.76) * mm, "radius": 3.18 * mm});
            skCircle(sketch, "E10.0.9.18", {"center": v(-53.88, 121.23) * mm, "radius": 3.18 * mm});
            skCircle(sketch, "E10.0.9.19", {"center": v(-53.88, 134.7) * mm, "radius": 3.18 * mm});
            skCircle(sketch, "E10.0.9.20", {"center": v(-53.88, 148.17) * mm, "radius": 3.18 * mm});
            skCircle(sketch, "E10.0.9.21", {"center": v(-53.88, 161.64) * mm, "radius": 3.18 * mm});
            skCircle(sketch, "E10.0.9.22", {"center": v(-53.88, 175.11) * mm, "radius": 3.18 * mm});
            skCircle(sketch, "E10.0.9.23", {"center": v(-53.88, 188.59) * mm, "radius": 3.18 * mm});
            skCircle(sketch, "E10.0.9.24", {"center": v(-53.88, 202.06) * mm, "radius": 3.18 * mm});
            skCircle(sketch, "E10.0.10.0", {"center": v(-40.41, -121.23) * mm, "radius": 3.18 * mm});
            skCircle(sketch, "E10.0.10.1", {"center": v(-40.41, -107.76) * mm, "radius": 3.18 * mm});
            skCircle(sketch, "E10.0.10.2", {"center": v(-40.41, -94.3) * mm, "radius": 3.18 * mm});
            skCircle(sketch, "E10.0.10.3", {"center": v(-40.41, -80.82) * mm, "radius": 3.18 * mm});
            skCircle(sketch, "E10.0.10.4", {"center": v(-40.41, -67.35) * mm, "radius": 3.18 * mm});
            skCircle(sketch, "E10.0.10.5", {"center": v(-40.41, -53.88) * mm, "radius": 3.18 * mm});
            skCircle(sketch, "E10.0.10.6", {"center": v(-40.41, -40.41) * mm, "radius": 3.18 * mm});
            skCircle(sketch, "E10.0.10.7", {"center": v(-40.41, -26.94) * mm, "radius": 3.18 * mm});
            skCircle(sketch, "E10.0.10.8", {"center": v(-40.41, -13.47) * mm, "radius": 3.18 * mm});
            skCircle(sketch, "E10.0.10.9", {"center": v(-40.41, 0) * mm, "radius": 3.18 * mm});
            skCircle(sketch, "E10.0.10.10", {"center": v(-40.41, 13.47) * mm, "radius": 3.18 * mm});
            skCircle(sketch, "E10.0.10.11", {"center": v(-40.41, 26.94) * mm, "radius": 3.18 * mm});
            skCircle(sketch, "E10.0.10.12", {"center": v(-40.41, 40.41) * mm, "radius": 3.18 * mm});
            skCircle(sketch, "E10.0.10.13", {"center": v(-40.41, 53.88) * mm, "radius": 3.18 * mm});
            skCircle(sketch, "E10.0.10.14", {"center": v(-40.41, 67.35) * mm, "radius": 3.18 * mm});
            skCircle(sketch, "E10.0.10.15", {"center": v(-40.41, 80.82) * mm, "radius": 3.18 * mm});
            skCircle(sketch, "E10.0.10.16", {"center": v(-40.41, 94.3) * mm, "radius": 3.18 * mm});
            skCircle(sketch, "E10.0.10.17", {"center": v(-40.41, 107.76) * mm, "radius": 3.18 * mm});
            skCircle(sketch, "E10.0.10.18", {"center": v(-40.41, 121.23) * mm, "radius": 3.18 * mm});
            skCircle(sketch, "E10.0.10.19", {"center": v(-40.41, 134.7) * mm, "radius": 3.18 * mm});
            skCircle(sketch, "E10.0.10.20", {"center": v(-40.41, 148.17) * mm, "radius": 3.18 * mm});
            skCircle(sketch, "E10.0.10.21", {"center": v(-40.41, 161.64) * mm, "radius": 3.18 * mm});
            skCircle(sketch, "E10.0.10.22", {"center": v(-40.41, 175.11) * mm, "radius": 3.18 * mm});
            skCircle(sketch, "E10.0.10.23", {"center": v(-40.41, 188.59) * mm, "radius": 3.18 * mm});
            skCircle(sketch, "E10.0.10.24", {"center": v(-40.41, 202.06) * mm, "radius": 3.18 * mm});
            skCircle(sketch, "E10.0.11.0", {"center": v(-26.94, -121.23) * mm, "radius": 3.18 * mm});
            skCircle(sketch, "E10.0.11.1", {"center": v(-26.94, -107.76) * mm, "radius": 3.18 * mm});
            skCircle(sketch, "E10.0.11.2", {"center": v(-26.94, -94.3) * mm, "radius": 3.18 * mm});
            skCircle(sketch, "E10.0.11.3", {"center": v(-26.94, -80.82) * mm, "radius": 3.18 * mm});
            skCircle(sketch, "E10.0.11.4", {"center": v(-26.94, -67.35) * mm, "radius": 3.18 * mm});
            skCircle(sketch, "E10.0.11.5", {"center": v(-26.94, -53.88) * mm, "radius": 3.18 * mm});
            skCircle(sketch, "E10.0.11.6", {"center": v(-26.94, -40.41) * mm, "radius": 3.18 * mm});
            skCircle(sketch, "E10.0.11.7", {"center": v(-26.94, -26.94) * mm, "radius": 3.18 * mm});
            skCircle(sketch, "E10.0.11.8", {"center": v(-26.94, -13.47) * mm, "radius": 3.18 * mm});
            skCircle(sketch, "E10.0.11.9", {"center": v(-26.94, 0) * mm, "radius": 3.18 * mm});
            skCircle(sketch, "E10.0.11.10", {"center": v(-26.94, 13.47) * mm, "radius": 3.18 * mm});
            skCircle(sketch, "E10.0.11.11", {"center": v(-26.94, 26.94) * mm, "radius": 3.18 * mm});
            skCircle(sketch, "E10.0.11.12", {"center": v(-26.94, 40.41) * mm, "radius": 3.18 * mm});
            skCircle(sketch, "E10.0.11.13", {"center": v(-26.94, 53.88) * mm, "radius": 3.18 * mm});
            skCircle(sketch, "E10.0.11.14", {"center": v(-26.94, 67.35) * mm, "radius": 3.18 * mm});
            skCircle(sketch, "E10.0.11.15", {"center": v(-26.94, 80.82) * mm, "radius": 3.18 * mm});
            skCircle(sketch, "E10.0.11.16", {"center": v(-26.94, 94.3) * mm, "radius": 3.18 * mm});
            skCircle(sketch, "E10.0.11.17", {"center": v(-26.94, 107.76) * mm, "radius": 3.18 * mm});
            skCircle(sketch, "E10.0.11.18", {"center": v(-26.94, 121.23) * mm, "radius": 3.18 * mm});
            skCircle(sketch, "E10.0.11.19", {"center": v(-26.94, 134.7) * mm, "radius": 3.18 * mm});
            skCircle(sketch, "E10.0.11.20", {"center": v(-26.94, 148.17) * mm, "radius": 3.18 * mm});
            skCircle(sketch, "E10.0.11.21", {"center": v(-26.94, 161.64) * mm, "radius": 3.18 * mm});
            skCircle(sketch, "E10.0.11.22", {"center": v(-26.94, 175.11) * mm, "radius": 3.18 * mm});
            skCircle(sketch, "E10.0.11.23", {"center": v(-26.94, 188.59) * mm, "radius": 3.18 * mm});
            skCircle(sketch, "E10.0.11.24", {"center": v(-26.94, 202.06) * mm, "radius": 3.18 * mm});
            skCircle(sketch, "E10.0.12.0", {"center": v(-13.47, -121.23) * mm, "radius": 3.18 * mm});
            skCircle(sketch, "E10.0.12.1", {"center": v(-13.47, -107.76) * mm, "radius": 3.18 * mm});
            skCircle(sketch, "E10.0.12.2", {"center": v(-13.47, -94.3) * mm, "radius": 3.18 * mm});
            skCircle(sketch, "E10.0.12.3", {"center": v(-13.47, -80.82) * mm, "radius": 3.18 * mm});
            skCircle(sketch, "E10.0.12.4", {"center": v(-13.47, -67.35) * mm, "radius": 3.18 * mm});
            skCircle(sketch, "E10.0.12.5", {"center": v(-13.47, -53.88) * mm, "radius": 3.18 * mm});
            skCircle(sketch, "E10.0.12.6", {"center": v(-13.47, -40.41) * mm, "radius": 3.18 * mm});
            skCircle(sketch, "E10.0.12.7", {"center": v(-13.47, -26.94) * mm, "radius": 3.18 * mm});
            skCircle(sketch, "E10.0.12.8", {"center": v(-13.47, -13.47) * mm, "radius": 3.18 * mm});
            skCircle(sketch, "E10.0.12.9", {"center": v(-13.47, 0) * mm, "radius": 3.18 * mm});
            skCircle(sketch, "E10.0.12.10", {"center": v(-13.47, 13.47) * mm, "radius": 3.18 * mm});
            skCircle(sketch, "E10.0.12.11", {"center": v(-13.47, 26.94) * mm, "radius": 3.18 * mm});
            skCircle(sketch, "E10.0.12.12", {"center": v(-13.47, 40.41) * mm, "radius": 3.18 * mm});
            skCircle(sketch, "E10.0.12.13", {"center": v(-13.47, 53.88) * mm, "radius": 3.18 * mm});
            skCircle(sketch, "E10.0.12.14", {"center": v(-13.47, 67.35) * mm, "radius": 3.18 * mm});
            skCircle(sketch, "E10.0.12.15", {"center": v(-13.47, 80.82) * mm, "radius": 3.18 * mm});
            skCircle(sketch, "E10.0.12.16", {"center": v(-13.47, 94.3) * mm, "radius": 3.18 * mm});
            skCircle(sketch, "E10.0.12.17", {"center": v(-13.47, 107.76) * mm, "radius": 3.18 * mm});
            skCircle(sketch, "E10.0.12.18", {"center": v(-13.47, 121.23) * mm, "radius": 3.18 * mm});
            skCircle(sketch, "E10.0.12.19", {"center": v(-13.47, 134.7) * mm, "radius": 3.18 * mm});
            skCircle(sketch, "E10.0.12.20", {"center": v(-13.47, 148.17) * mm, "radius": 3.18 * mm});
            skCircle(sketch, "E10.0.12.21", {"center": v(-13.47, 161.64) * mm, "radius": 3.18 * mm});
            skCircle(sketch, "E10.0.12.22", {"center": v(-13.47, 175.11) * mm, "radius": 3.18 * mm});
            skCircle(sketch, "E10.0.12.23", {"center": v(-13.47, 188.59) * mm, "radius": 3.18 * mm});
            skCircle(sketch, "E10.0.12.24", {"center": v(-13.47, 202.06) * mm, "radius": 3.18 * mm});
            skCircle(sketch, "E10.0.13.0", {"center": v(0, -121.23) * mm, "radius": 3.18 * mm});
            skCircle(sketch, "E10.0.13.1", {"center": v(0, -107.76) * mm, "radius": 3.18 * mm});
            skCircle(sketch, "E10.0.13.2", {"center": v(0, -94.3) * mm, "radius": 3.18 * mm});
            skCircle(sketch, "E10.0.13.3", {"center": v(0, -80.82) * mm, "radius": 3.18 * mm});
            skCircle(sketch, "E10.0.13.4", {"center": v(0, -67.35) * mm, "radius": 3.18 * mm});
            skCircle(sketch, "E10.0.13.5", {"center": v(0, -53.88) * mm, "radius": 3.18 * mm});
            skCircle(sketch, "E10.0.13.6", {"center": v(0, -40.41) * mm, "radius": 3.18 * mm});
            skCircle(sketch, "E10.0.13.7", {"center": v(0, -26.94) * mm, "radius": 3.18 * mm});
            skCircle(sketch, "E10.0.13.8", {"center": v(0, -13.47) * mm, "radius": 3.18 * mm});
            skCircle(sketch, "E10.0.13.9", {"center": v(0, 0) * mm, "radius": 3.18 * mm});
            skCircle(sketch, "E10.0.13.10", {"center": v(0, 13.47) * mm, "radius": 3.18 * mm});
            skCircle(sketch, "E10.0.13.11", {"center": v(0, 26.94) * mm, "radius": 3.18 * mm});
            skCircle(sketch, "E10.0.13.12", {"center": v(0, 40.41) * mm, "radius": 3.18 * mm});
            skCircle(sketch, "E10.0.13.13", {"center": v(0, 53.88) * mm, "radius": 3.18 * mm});
            skCircle(sketch, "E10.0.13.14", {"center": v(0, 67.35) * mm, "radius": 3.18 * mm});
            skCircle(sketch, "E10.0.13.15", {"center": v(0, 80.82) * mm, "radius": 3.18 * mm});
            skCircle(sketch, "E10.0.13.16", {"center": v(0, 94.3) * mm, "radius": 3.18 * mm});
            skCircle(sketch, "E10.0.13.17", {"center": v(0, 107.76) * mm, "radius": 3.18 * mm});
            skCircle(sketch, "E10.0.13.18", {"center": v(0, 121.23) * mm, "radius": 3.18 * mm});
            skCircle(sketch, "E10.0.13.19", {"center": v(0, 134.7) * mm, "radius": 3.18 * mm});
            skCircle(sketch, "E10.0.13.20", {"center": v(0, 148.17) * mm, "radius": 3.18 * mm});
            skCircle(sketch, "E10.0.13.21", {"center": v(0, 161.64) * mm, "radius": 3.18 * mm});
            skCircle(sketch, "E10.0.13.22", {"center": v(0, 175.11) * mm, "radius": 3.18 * mm});
            skCircle(sketch, "E10.0.13.23", {"center": v(0, 188.59) * mm, "radius": 3.18 * mm});
            skCircle(sketch, "E10.0.13.24", {"center": v(0, 202.06) * mm, "radius": 3.18 * mm});
            skCircle(sketch, "E10.0.14.0", {"center": v(13.47, -121.23) * mm, "radius": 3.18 * mm});
            skCircle(sketch, "E10.0.14.1", {"center": v(13.47, -107.76) * mm, "radius": 3.18 * mm});
            skCircle(sketch, "E10.0.14.2", {"center": v(13.47, -94.3) * mm, "radius": 3.18 * mm});
            skCircle(sketch, "E10.0.14.3", {"center": v(13.47, -80.82) * mm, "radius": 3.18 * mm});
            skCircle(sketch, "E10.0.14.4", {"center": v(13.47, -67.35) * mm, "radius": 3.18 * mm});
            skCircle(sketch, "E10.0.14.5", {"center": v(13.47, -53.88) * mm, "radius": 3.18 * mm});
            skCircle(sketch, "E10.0.14.6", {"center": v(13.47, -40.41) * mm, "radius": 3.18 * mm});
            skCircle(sketch, "E10.0.14.7", {"center": v(13.47, -26.94) * mm, "radius": 3.18 * mm});
            skCircle(sketch, "E10.0.14.8", {"center": v(13.47, -13.47) * mm, "radius": 3.18 * mm});
            skCircle(sketch, "E10.0.14.9", {"center": v(13.47, 0) * mm, "radius": 3.18 * mm});
            skCircle(sketch, "E10.0.14.10", {"center": v(13.47, 13.47) * mm, "radius": 3.18 * mm});
            skCircle(sketch, "E10.0.14.11", {"center": v(13.47, 26.94) * mm, "radius": 3.18 * mm});
            skCircle(sketch, "E10.0.14.12", {"center": v(13.47, 40.41) * mm, "radius": 3.18 * mm});
            skCircle(sketch, "E10.0.14.13", {"center": v(13.47, 53.88) * mm, "radius": 3.18 * mm});
            skCircle(sketch, "E10.0.14.14", {"center": v(13.47, 67.35) * mm, "radius": 3.18 * mm});
            skCircle(sketch, "E10.0.14.15", {"center": v(13.47, 80.82) * mm, "radius": 3.18 * mm});
            skCircle(sketch, "E10.0.14.16", {"center": v(13.47, 94.3) * mm, "radius": 3.18 * mm});
            skCircle(sketch, "E10.0.14.17", {"center": v(13.47, 107.76) * mm, "radius": 3.18 * mm});
            skCircle(sketch, "E10.0.14.18", {"center": v(13.47, 121.23) * mm, "radius": 3.18 * mm});
            skCircle(sketch, "E10.0.14.19", {"center": v(13.47, 134.7) * mm, "radius": 3.18 * mm});
            skCircle(sketch, "E10.0.14.20", {"center": v(13.47, 148.17) * mm, "radius": 3.18 * mm});
            skCircle(sketch, "E10.0.14.21", {"center": v(13.47, 161.64) * mm, "radius": 3.18 * mm});
            skCircle(sketch, "E10.0.14.22", {"center": v(13.47, 175.11) * mm, "radius": 3.18 * mm});
            skCircle(sketch, "E10.0.14.23", {"center": v(13.47, 188.59) * mm, "radius": 3.18 * mm});
            skCircle(sketch, "E10.0.14.24", {"center": v(13.47, 202.06) * mm, "radius": 3.18 * mm});
            skCircle(sketch, "E10.0.15.0", {"center": v(26.94, -121.23) * mm, "radius": 3.18 * mm});
            skCircle(sketch, "E10.0.15.1", {"center": v(26.94, -107.76) * mm, "radius": 3.18 * mm});
            skCircle(sketch, "E10.0.15.2", {"center": v(26.94, -94.3) * mm, "radius": 3.18 * mm});
            skCircle(sketch, "E10.0.15.3", {"center": v(26.94, -80.82) * mm, "radius": 3.18 * mm});
            skCircle(sketch, "E10.0.15.4", {"center": v(26.94, -67.35) * mm, "radius": 3.18 * mm});
            skCircle(sketch, "E10.0.15.5", {"center": v(26.94, -53.88) * mm, "radius": 3.18 * mm});
            skCircle(sketch, "E10.0.15.6", {"center": v(26.94, -40.41) * mm, "radius": 3.18 * mm});
            skCircle(sketch, "E10.0.15.7", {"center": v(26.94, -26.94) * mm, "radius": 3.18 * mm});
            skCircle(sketch, "E10.0.15.8", {"center": v(26.94, -13.47) * mm, "radius": 3.18 * mm});
            skCircle(sketch, "E10.0.15.9", {"center": v(26.94, 0) * mm, "radius": 3.18 * mm});
            skCircle(sketch, "E10.0.15.10", {"center": v(26.94, 13.47) * mm, "radius": 3.18 * mm});
            skCircle(sketch, "E10.0.15.11", {"center": v(26.94, 26.94) * mm, "radius": 3.18 * mm});
            skCircle(sketch, "E10.0.15.12", {"center": v(26.94, 40.41) * mm, "radius": 3.18 * mm});
            skCircle(sketch, "E10.0.15.13", {"center": v(26.94, 53.88) * mm, "radius": 3.18 * mm});
            skCircle(sketch, "E10.0.15.14", {"center": v(26.94, 67.35) * mm, "radius": 3.18 * mm});
            skCircle(sketch, "E10.0.15.15", {"center": v(26.94, 80.82) * mm, "radius": 3.18 * mm});
            skCircle(sketch, "E10.0.15.16", {"center": v(26.94, 94.3) * mm, "radius": 3.18 * mm});
            skCircle(sketch, "E10.0.15.17", {"center": v(26.94, 107.76) * mm, "radius": 3.18 * mm});
            skCircle(sketch, "E10.0.15.18", {"center": v(26.94, 121.23) * mm, "radius": 3.18 * mm});
            skCircle(sketch, "E10.0.15.19", {"center": v(26.94, 134.7) * mm, "radius": 3.18 * mm});
            skCircle(sketch, "E10.0.15.20", {"center": v(26.94, 148.17) * mm, "radius": 3.18 * mm});
            skCircle(sketch, "E10.0.15.21", {"center": v(26.94, 161.64) * mm, "radius": 3.18 * mm});
            skCircle(sketch, "E10.0.15.22", {"center": v(26.94, 175.11) * mm, "radius": 3.18 * mm});
            skCircle(sketch, "E10.0.15.23", {"center": v(26.94, 188.59) * mm, "radius": 3.18 * mm});
            skCircle(sketch, "E10.0.15.24", {"center": v(26.94, 202.06) * mm, "radius": 3.18 * mm});
            skCircle(sketch, "E10.0.16.0", {"center": v(40.41, -121.23) * mm, "radius": 3.18 * mm});
            skCircle(sketch, "E10.0.16.1", {"center": v(40.41, -107.76) * mm, "radius": 3.18 * mm});
            skCircle(sketch, "E10.0.16.2", {"center": v(40.41, -94.3) * mm, "radius": 3.18 * mm});
            skCircle(sketch, "E10.0.16.3", {"center": v(40.41, -80.82) * mm, "radius": 3.18 * mm});
            skCircle(sketch, "E10.0.16.4", {"center": v(40.41, -67.35) * mm, "radius": 3.18 * mm});
            skCircle(sketch, "E10.0.16.5", {"center": v(40.41, -53.88) * mm, "radius": 3.18 * mm});
            skCircle(sketch, "E10.0.16.6", {"center": v(40.41, -40.41) * mm, "radius": 3.18 * mm});
            skCircle(sketch, "E10.0.16.7", {"center": v(40.41, -26.94) * mm, "radius": 3.18 * mm});
            skCircle(sketch, "E10.0.16.8", {"center": v(40.41, -13.47) * mm, "radius": 3.18 * mm});
            skCircle(sketch, "E10.0.16.9", {"center": v(40.41, 0) * mm, "radius": 3.18 * mm});
            skCircle(sketch, "E10.0.16.10", {"center": v(40.41, 13.47) * mm, "radius": 3.18 * mm});
            skCircle(sketch, "E10.0.16.11", {"center": v(40.41, 26.94) * mm, "radius": 3.18 * mm});
            skCircle(sketch, "E10.0.16.12", {"center": v(40.41, 40.41) * mm, "radius": 3.18 * mm});
            skCircle(sketch, "E10.0.16.13", {"center": v(40.41, 53.88) * mm, "radius": 3.18 * mm});
            skCircle(sketch, "E10.0.16.14", {"center": v(40.41, 67.35) * mm, "radius": 3.18 * mm});
            skCircle(sketch, "E10.0.16.15", {"center": v(40.41, 80.82) * mm, "radius": 3.18 * mm});
            skCircle(sketch, "E10.0.16.16", {"center": v(40.41, 94.3) * mm, "radius": 3.18 * mm});
            skCircle(sketch, "E10.0.16.17", {"center": v(40.41, 107.76) * mm, "radius": 3.18 * mm});
            skCircle(sketch, "E10.0.16.18", {"center": v(40.41, 121.23) * mm, "radius": 3.18 * mm});
            skCircle(sketch, "E10.0.16.19", {"center": v(40.41, 134.7) * mm, "radius": 3.18 * mm});
            skCircle(sketch, "E10.0.16.20", {"center": v(40.41, 148.17) * mm, "radius": 3.18 * mm});
            skCircle(sketch, "E10.0.16.21", {"center": v(40.41, 161.64) * mm, "radius": 3.18 * mm});
            skCircle(sketch, "E10.0.16.22", {"center": v(40.41, 175.11) * mm, "radius": 3.18 * mm});
            skCircle(sketch, "E10.0.16.23", {"center": v(40.41, 188.59) * mm, "radius": 3.18 * mm});
            skCircle(sketch, "E10.0.16.24", {"center": v(40.41, 202.06) * mm, "radius": 3.18 * mm});
            skCircle(sketch, "E10.0.17.0", {"center": v(53.88, -121.23) * mm, "radius": 3.18 * mm});
            skCircle(sketch, "E10.0.17.1", {"center": v(53.88, -107.76) * mm, "radius": 3.18 * mm});
            skCircle(sketch, "E10.0.17.2", {"center": v(53.88, -94.3) * mm, "radius": 3.18 * mm});
            skCircle(sketch, "E10.0.17.3", {"center": v(53.88, -80.82) * mm, "radius": 3.18 * mm});
            skCircle(sketch, "E10.0.17.4", {"center": v(53.88, -67.35) * mm, "radius": 3.18 * mm});
            skCircle(sketch, "E10.0.17.5", {"center": v(53.88, -53.88) * mm, "radius": 3.18 * mm});
            skCircle(sketch, "E10.0.17.6", {"center": v(53.88, -40.41) * mm, "radius": 3.18 * mm});
            skCircle(sketch, "E10.0.17.7", {"center": v(53.88, -26.94) * mm, "radius": 3.18 * mm});
            skCircle(sketch, "E10.0.17.8", {"center": v(53.88, -13.47) * mm, "radius": 3.18 * mm});
            skCircle(sketch, "E10.0.17.9", {"center": v(53.88, 0) * mm, "radius": 3.18 * mm});
            skCircle(sketch, "E10.0.17.10", {"center": v(53.88, 13.47) * mm, "radius": 3.18 * mm});
            skCircle(sketch, "E10.0.17.11", {"center": v(53.88, 26.94) * mm, "radius": 3.18 * mm});
            skCircle(sketch, "E10.0.17.12", {"center": v(53.88, 40.41) * mm, "radius": 3.18 * mm});
            skCircle(sketch, "E10.0.17.13", {"center": v(53.88, 53.88) * mm, "radius": 3.18 * mm});
            skCircle(sketch, "E10.0.17.14", {"center": v(53.88, 67.35) * mm, "radius": 3.18 * mm});
            skCircle(sketch, "E10.0.17.15", {"center": v(53.88, 80.82) * mm, "radius": 3.18 * mm});
            skCircle(sketch, "E10.0.17.16", {"center": v(53.88, 94.3) * mm, "radius": 3.18 * mm});
            skCircle(sketch, "E10.0.17.17", {"center": v(53.88, 107.76) * mm, "radius": 3.18 * mm});
            skCircle(sketch, "E10.0.17.18", {"center": v(53.88, 121.23) * mm, "radius": 3.18 * mm});
            skCircle(sketch, "E10.0.17.19", {"center": v(53.88, 134.7) * mm, "radius": 3.18 * mm});
            skCircle(sketch, "E10.0.17.20", {"center": v(53.88, 148.17) * mm, "radius": 3.18 * mm});
            skCircle(sketch, "E10.0.17.21", {"center": v(53.88, 161.64) * mm, "radius": 3.18 * mm});
            skCircle(sketch, "E10.0.17.22", {"center": v(53.88, 175.11) * mm, "radius": 3.18 * mm});
            skCircle(sketch, "E10.0.17.23", {"center": v(53.88, 188.59) * mm, "radius": 3.18 * mm});
            skCircle(sketch, "E10.0.17.24", {"center": v(53.88, 202.06) * mm, "radius": 3.18 * mm});
            skCircle(sketch, "E10.0.18.0", {"center": v(67.35, -121.23) * mm, "radius": 3.18 * mm});
            skCircle(sketch, "E10.0.18.1", {"center": v(67.35, -107.76) * mm, "radius": 3.18 * mm});
            skCircle(sketch, "E10.0.18.2", {"center": v(67.35, -94.3) * mm, "radius": 3.18 * mm});
            skCircle(sketch, "E10.0.18.3", {"center": v(67.35, -80.82) * mm, "radius": 3.18 * mm});
            skCircle(sketch, "E10.0.18.4", {"center": v(67.35, -67.35) * mm, "radius": 3.18 * mm});
            skCircle(sketch, "E10.0.18.5", {"center": v(67.35, -53.88) * mm, "radius": 3.18 * mm});
            skCircle(sketch, "E10.0.18.6", {"center": v(67.35, -40.41) * mm, "radius": 3.18 * mm});
            skCircle(sketch, "E10.0.18.7", {"center": v(67.35, -26.94) * mm, "radius": 3.18 * mm});
            skCircle(sketch, "E10.0.18.8", {"center": v(67.35, -13.47) * mm, "radius": 3.18 * mm});
            skCircle(sketch, "E10.0.18.9", {"center": v(67.35, 0) * mm, "radius": 3.18 * mm});
            skCircle(sketch, "E10.0.18.10", {"center": v(67.35, 13.47) * mm, "radius": 3.18 * mm});
            skCircle(sketch, "E10.0.18.11", {"center": v(67.35, 26.94) * mm, "radius": 3.18 * mm});
            skCircle(sketch, "E10.0.18.12", {"center": v(67.35, 40.41) * mm, "radius": 3.18 * mm});
            skCircle(sketch, "E10.0.18.13", {"center": v(67.35, 53.88) * mm, "radius": 3.18 * mm});
            skCircle(sketch, "E10.0.18.14", {"center": v(67.35, 67.35) * mm, "radius": 3.18 * mm});
            skCircle(sketch, "E10.0.18.15", {"center": v(67.35, 80.82) * mm, "radius": 3.18 * mm});
            skCircle(sketch, "E10.0.18.16", {"center": v(67.35, 94.3) * mm, "radius": 3.18 * mm});
            skCircle(sketch, "E10.0.18.17", {"center": v(67.35, 107.76) * mm, "radius": 3.18 * mm});
            skCircle(sketch, "E10.0.18.18", {"center": v(67.35, 121.23) * mm, "radius": 3.18 * mm});
            skCircle(sketch, "E10.0.18.19", {"center": v(67.35, 134.7) * mm, "radius": 3.18 * mm});
            skCircle(sketch, "E10.0.18.20", {"center": v(67.35, 148.17) * mm, "radius": 3.18 * mm});
            skCircle(sketch, "E10.0.18.21", {"center": v(67.35, 161.64) * mm, "radius": 3.18 * mm});
            skCircle(sketch, "E10.0.18.22", {"center": v(67.35, 175.11) * mm, "radius": 3.18 * mm});
            skCircle(sketch, "E10.0.18.23", {"center": v(67.35, 188.59) * mm, "radius": 3.18 * mm});
            skCircle(sketch, "E10.0.18.24", {"center": v(67.35, 202.06) * mm, "radius": 3.18 * mm});
            skCircle(sketch, "E10.0.19.0", {"center": v(80.82, -121.23) * mm, "radius": 3.18 * mm});
            skCircle(sketch, "E10.0.19.1", {"center": v(80.82, -107.76) * mm, "radius": 3.18 * mm});
            skCircle(sketch, "E10.0.19.2", {"center": v(80.82, -94.3) * mm, "radius": 3.18 * mm});
            skCircle(sketch, "E10.0.19.3", {"center": v(80.82, -80.82) * mm, "radius": 3.18 * mm});
            skCircle(sketch, "E10.0.19.4", {"center": v(80.82, -67.35) * mm, "radius": 3.18 * mm});
            skCircle(sketch, "E10.0.19.5", {"center": v(80.82, -53.88) * mm, "radius": 3.18 * mm});
            skCircle(sketch, "E10.0.19.6", {"center": v(80.82, -40.41) * mm, "radius": 3.18 * mm});
            skCircle(sketch, "E10.0.19.7", {"center": v(80.82, -26.94) * mm, "radius": 3.18 * mm});
            skCircle(sketch, "E10.0.19.8", {"center": v(80.82, -13.47) * mm, "radius": 3.18 * mm});
            skCircle(sketch, "E10.0.19.9", {"center": v(80.82, 0) * mm, "radius": 3.18 * mm});
            skCircle(sketch, "E10.0.19.10", {"center": v(80.82, 13.47) * mm, "radius": 3.18 * mm});
            skCircle(sketch, "E10.0.19.11", {"center": v(80.82, 26.94) * mm, "radius": 3.18 * mm});
            skCircle(sketch, "E10.0.19.12", {"center": v(80.82, 40.41) * mm, "radius": 3.18 * mm});
            skCircle(sketch, "E10.0.19.13", {"center": v(80.82, 53.88) * mm, "radius": 3.18 * mm});
            skCircle(sketch, "E10.0.19.14", {"center": v(80.82, 67.35) * mm, "radius": 3.18 * mm});
            skCircle(sketch, "E10.0.19.15", {"center": v(80.82, 80.82) * mm, "radius": 3.18 * mm});
            skCircle(sketch, "E10.0.19.16", {"center": v(80.82, 94.3) * mm, "radius": 3.18 * mm});
            skCircle(sketch, "E10.0.19.17", {"center": v(80.82, 107.76) * mm, "radius": 3.18 * mm});
            skCircle(sketch, "E10.0.19.18", {"center": v(80.82, 121.23) * mm, "radius": 3.18 * mm});
            skCircle(sketch, "E10.0.19.19", {"center": v(80.82, 134.7) * mm, "radius": 3.18 * mm});
            skCircle(sketch, "E10.0.19.20", {"center": v(80.82, 148.17) * mm, "radius": 3.18 * mm});
            skCircle(sketch, "E10.0.19.21", {"center": v(80.82, 161.64) * mm, "radius": 3.18 * mm});
            skCircle(sketch, "E10.0.19.22", {"center": v(80.82, 175.11) * mm, "radius": 3.18 * mm});
            skCircle(sketch, "E10.0.19.23", {"center": v(80.82, 188.59) * mm, "radius": 3.18 * mm});
            skCircle(sketch, "E10.0.19.24", {"center": v(80.82, 202.06) * mm, "radius": 3.18 * mm});
            skCircle(sketch, "E10.0.20.0", {"center": v(94.3, -121.23) * mm, "radius": 3.18 * mm});
            skCircle(sketch, "E10.0.20.1", {"center": v(94.3, -107.76) * mm, "radius": 3.18 * mm});
            skCircle(sketch, "E10.0.20.2", {"center": v(94.3, -94.3) * mm, "radius": 3.18 * mm});
            skCircle(sketch, "E10.0.20.3", {"center": v(94.3, -80.82) * mm, "radius": 3.18 * mm});
            skCircle(sketch, "E10.0.20.4", {"center": v(94.3, -67.35) * mm, "radius": 3.18 * mm});
            skCircle(sketch, "E10.0.20.5", {"center": v(94.3, -53.88) * mm, "radius": 3.18 * mm});
            skCircle(sketch, "E10.0.20.6", {"center": v(94.3, -40.41) * mm, "radius": 3.18 * mm});
            skCircle(sketch, "E10.0.20.7", {"center": v(94.3, -26.94) * mm, "radius": 3.18 * mm});
            skCircle(sketch, "E10.0.20.8", {"center": v(94.3, -13.47) * mm, "radius": 3.18 * mm});
            skCircle(sketch, "E10.0.20.9", {"center": v(94.3, 0) * mm, "radius": 3.18 * mm});
            skCircle(sketch, "E10.0.20.10", {"center": v(94.3, 13.47) * mm, "radius": 3.18 * mm});
            skCircle(sketch, "E10.0.20.11", {"center": v(94.3, 26.94) * mm, "radius": 3.18 * mm});
            skCircle(sketch, "E10.0.20.12", {"center": v(94.3, 40.41) * mm, "radius": 3.18 * mm});
            skCircle(sketch, "E10.0.20.13", {"center": v(94.3, 53.88) * mm, "radius": 3.18 * mm});
            skCircle(sketch, "E10.0.20.14", {"center": v(94.3, 67.35) * mm, "radius": 3.18 * mm});
            skCircle(sketch, "E10.0.20.15", {"center": v(94.3, 80.82) * mm, "radius": 3.18 * mm});
            skCircle(sketch, "E10.0.20.16", {"center": v(94.3, 94.3) * mm, "radius": 3.18 * mm});
            skCircle(sketch, "E10.0.20.17", {"center": v(94.3, 107.76) * mm, "radius": 3.18 * mm});
            skCircle(sketch, "E10.0.20.18", {"center": v(94.3, 121.23) * mm, "radius": 3.18 * mm});
            skCircle(sketch, "E10.0.20.19", {"center": v(94.3, 134.7) * mm, "radius": 3.18 * mm});
            skCircle(sketch, "E10.0.20.20", {"center": v(94.3, 148.17) * mm, "radius": 3.18 * mm});
            skCircle(sketch, "E10.0.20.21", {"center": v(94.3, 161.64) * mm, "radius": 3.18 * mm});
            skCircle(sketch, "E10.0.20.22", {"center": v(94.3, 175.11) * mm, "radius": 3.18 * mm});
            skCircle(sketch, "E10.0.20.23", {"center": v(94.3, 188.59) * mm, "radius": 3.18 * mm});
            skCircle(sketch, "E10.0.20.24", {"center": v(94.3, 202.06) * mm, "radius": 3.18 * mm});
            skCircle(sketch, "E10.0.21.0", {"center": v(107.76, -121.23) * mm, "radius": 3.18 * mm});
            skCircle(sketch, "E10.0.21.1", {"center": v(107.76, -107.76) * mm, "radius": 3.18 * mm});
            skCircle(sketch, "E10.0.21.2", {"center": v(107.76, -94.3) * mm, "radius": 3.18 * mm});
            skCircle(sketch, "E10.0.21.3", {"center": v(107.76, -80.82) * mm, "radius": 3.18 * mm});
            skCircle(sketch, "E10.0.21.4", {"center": v(107.76, -67.35) * mm, "radius": 3.18 * mm});
            skCircle(sketch, "E10.0.21.5", {"center": v(107.76, -53.88) * mm, "radius": 3.18 * mm});
            skCircle(sketch, "E10.0.21.6", {"center": v(107.76, -40.41) * mm, "radius": 3.18 * mm});
            skCircle(sketch, "E10.0.21.7", {"center": v(107.76, -26.94) * mm, "radius": 3.18 * mm});
            skCircle(sketch, "E10.0.21.8", {"center": v(107.76, -13.47) * mm, "radius": 3.18 * mm});
            skCircle(sketch, "E10.0.21.9", {"center": v(107.76, 0) * mm, "radius": 3.18 * mm});
            skCircle(sketch, "E10.0.21.10", {"center": v(107.76, 13.47) * mm, "radius": 3.18 * mm});
            skCircle(sketch, "E10.0.21.11", {"center": v(107.76, 26.94) * mm, "radius": 3.18 * mm});
            skCircle(sketch, "E10.0.21.12", {"center": v(107.76, 40.41) * mm, "radius": 3.18 * mm});
            skCircle(sketch, "E10.0.21.13", {"center": v(107.76, 53.88) * mm, "radius": 3.18 * mm});
            skCircle(sketch, "E10.0.21.14", {"center": v(107.76, 67.35) * mm, "radius": 3.18 * mm});
            skCircle(sketch, "E10.0.21.15", {"center": v(107.76, 80.82) * mm, "radius": 3.18 * mm});
            skCircle(sketch, "E10.0.21.16", {"center": v(107.76, 94.3) * mm, "radius": 3.18 * mm});
            skCircle(sketch, "E10.0.21.17", {"center": v(107.76, 107.76) * mm, "radius": 3.18 * mm});
            skCircle(sketch, "E10.0.21.18", {"center": v(107.76, 121.23) * mm, "radius": 3.18 * mm});
            skCircle(sketch, "E10.0.21.19", {"center": v(107.76, 134.7) * mm, "radius": 3.18 * mm});
            skCircle(sketch, "E10.0.21.20", {"center": v(107.76, 148.17) * mm, "radius": 3.18 * mm});
            skCircle(sketch, "E10.0.21.21", {"center": v(107.76, 161.64) * mm, "radius": 3.18 * mm});
            skCircle(sketch, "E10.0.21.22", {"center": v(107.76, 175.11) * mm, "radius": 3.18 * mm});
            skCircle(sketch, "E10.0.21.23", {"center": v(107.76, 188.59) * mm, "radius": 3.18 * mm});
            skCircle(sketch, "E10.0.21.24", {"center": v(107.76, 202.06) * mm, "radius": 3.18 * mm});
            skCircle(sketch, "E10.0.22.0", {"center": v(121.23, -121.23) * mm, "radius": 3.18 * mm});
            skCircle(sketch, "E10.0.22.1", {"center": v(121.23, -107.76) * mm, "radius": 3.18 * mm});
            skCircle(sketch, "E10.0.22.2", {"center": v(121.23, -94.3) * mm, "radius": 3.18 * mm});
            skCircle(sketch, "E10.0.22.3", {"center": v(121.23, -80.82) * mm, "radius": 3.18 * mm});
            skCircle(sketch, "E10.0.22.4", {"center": v(121.23, -67.35) * mm, "radius": 3.18 * mm});
            skCircle(sketch, "E10.0.22.5", {"center": v(121.23, -53.88) * mm, "radius": 3.18 * mm});
            skCircle(sketch, "E10.0.22.6", {"center": v(121.23, -40.41) * mm, "radius": 3.18 * mm});
            skCircle(sketch, "E10.0.22.7", {"center": v(121.23, -26.94) * mm, "radius": 3.18 * mm});
            skCircle(sketch, "E10.0.22.8", {"center": v(121.23, -13.47) * mm, "radius": 3.18 * mm});
            skCircle(sketch, "E10.0.22.9", {"center": v(121.23, 0) * mm, "radius": 3.18 * mm});
            skCircle(sketch, "E10.0.22.10", {"center": v(121.23, 13.47) * mm, "radius": 3.18 * mm});
            skCircle(sketch, "E10.0.22.11", {"center": v(121.23, 26.94) * mm, "radius": 3.18 * mm});
            skCircle(sketch, "E10.0.22.12", {"center": v(121.23, 40.41) * mm, "radius": 3.18 * mm});
            skCircle(sketch, "E10.0.22.13", {"center": v(121.23, 53.88) * mm, "radius": 3.18 * mm});
            skCircle(sketch, "E10.0.22.14", {"center": v(121.23, 67.35) * mm, "radius": 3.18 * mm});
            skCircle(sketch, "E10.0.22.15", {"center": v(121.23, 80.82) * mm, "radius": 3.18 * mm});
            skCircle(sketch, "E10.0.22.16", {"center": v(121.23, 94.3) * mm, "radius": 3.18 * mm});
            skCircle(sketch, "E10.0.22.17", {"center": v(121.23, 107.76) * mm, "radius": 3.18 * mm});
            skCircle(sketch, "E10.0.22.18", {"center": v(121.23, 121.23) * mm, "radius": 3.18 * mm});
            skCircle(sketch, "E10.0.22.19", {"center": v(121.23, 134.7) * mm, "radius": 3.18 * mm});
            skCircle(sketch, "E10.0.22.20", {"center": v(121.23, 148.17) * mm, "radius": 3.18 * mm});
            skCircle(sketch, "E10.0.22.21", {"center": v(121.23, 161.64) * mm, "radius": 3.18 * mm});
            skCircle(sketch, "E10.0.22.22", {"center": v(121.23, 175.11) * mm, "radius": 3.18 * mm});
            skCircle(sketch, "E10.0.22.23", {"center": v(121.23, 188.59) * mm, "radius": 3.18 * mm});
            skCircle(sketch, "E10.0.22.24", {"center": v(121.23, 202.06) * mm, "radius": 3.18 * mm});
            skCircle(sketch, "E10.0.23.0", {"center": v(134.7, -121.23) * mm, "radius": 3.18 * mm});
            skCircle(sketch, "E10.0.23.1", {"center": v(134.7, -107.76) * mm, "radius": 3.18 * mm});
            skCircle(sketch, "E10.0.23.2", {"center": v(134.7, -94.3) * mm, "radius": 3.18 * mm});
            skCircle(sketch, "E10.0.23.3", {"center": v(134.7, -80.82) * mm, "radius": 3.18 * mm});
            skCircle(sketch, "E10.0.23.4", {"center": v(134.7, -67.35) * mm, "radius": 3.18 * mm});
            skCircle(sketch, "E10.0.23.5", {"center": v(134.7, -53.88) * mm, "radius": 3.18 * mm});
            skCircle(sketch, "E10.0.23.6", {"center": v(134.7, -40.41) * mm, "radius": 3.18 * mm});
            skCircle(sketch, "E10.0.23.7", {"center": v(134.7, -26.94) * mm, "radius": 3.18 * mm});
            skCircle(sketch, "E10.0.23.8", {"center": v(134.7, -13.47) * mm, "radius": 3.18 * mm});
            skCircle(sketch, "E10.0.23.9", {"center": v(134.7, 0) * mm, "radius": 3.18 * mm});
            skCircle(sketch, "E10.0.23.10", {"center": v(134.7, 13.47) * mm, "radius": 3.18 * mm});
            skCircle(sketch, "E10.0.23.11", {"center": v(134.7, 26.94) * mm, "radius": 3.18 * mm});
            skCircle(sketch, "E10.0.23.12", {"center": v(134.7, 40.41) * mm, "radius": 3.18 * mm});
            skCircle(sketch, "E10.0.23.13", {"center": v(134.7, 53.88) * mm, "radius": 3.18 * mm});
            skCircle(sketch, "E10.0.23.14", {"center": v(134.7, 67.35) * mm, "radius": 3.18 * mm});
            skCircle(sketch, "E10.0.23.15", {"center": v(134.7, 80.82) * mm, "radius": 3.18 * mm});
            skCircle(sketch, "E10.0.23.16", {"center": v(134.7, 94.3) * mm, "radius": 3.18 * mm});
            skCircle(sketch, "E10.0.23.17", {"center": v(134.7, 107.76) * mm, "radius": 3.18 * mm});
            skCircle(sketch, "E10.0.23.18", {"center": v(134.7, 121.23) * mm, "radius": 3.18 * mm});
            skCircle(sketch, "E10.0.23.19", {"center": v(134.7, 134.7) * mm, "radius": 3.18 * mm});
            skCircle(sketch, "E10.0.23.20", {"center": v(134.7, 148.17) * mm, "radius": 3.18 * mm});
            skCircle(sketch, "E10.0.23.21", {"center": v(134.7, 161.64) * mm, "radius": 3.18 * mm});
            skCircle(sketch, "E10.0.23.22", {"center": v(134.7, 175.11) * mm, "radius": 3.18 * mm});
            skCircle(sketch, "E10.0.23.23", {"center": v(134.7, 188.59) * mm, "radius": 3.18 * mm});
            skCircle(sketch, "E10.0.23.24", {"center": v(134.7, 202.06) * mm, "radius": 3.18 * mm});
            skCircle(sketch, "E10.0.24.0", {"center": v(148.17, -121.23) * mm, "radius": 3.18 * mm});
            skCircle(sketch, "E10.0.24.1", {"center": v(148.17, -107.76) * mm, "radius": 3.18 * mm});
            skCircle(sketch, "E10.0.24.2", {"center": v(148.17, -94.3) * mm, "radius": 3.18 * mm});
            skCircle(sketch, "E10.0.24.3", {"center": v(148.17, -80.82) * mm, "radius": 3.18 * mm});
            skCircle(sketch, "E10.0.24.4", {"center": v(148.17, -67.35) * mm, "radius": 3.18 * mm});
            skCircle(sketch, "E10.0.24.5", {"center": v(148.17, -53.88) * mm, "radius": 3.18 * mm});
            skCircle(sketch, "E10.0.24.6", {"center": v(148.17, -40.41) * mm, "radius": 3.18 * mm});
            skCircle(sketch, "E10.0.24.7", {"center": v(148.17, -26.94) * mm, "radius": 3.18 * mm});
            skCircle(sketch, "E10.0.24.8", {"center": v(148.17, -13.47) * mm, "radius": 3.18 * mm});
            skCircle(sketch, "E10.0.24.9", {"center": v(148.17, 0) * mm, "radius": 3.18 * mm});
            skCircle(sketch, "E10.0.24.10", {"center": v(148.17, 13.47) * mm, "radius": 3.18 * mm});
            skCircle(sketch, "E10.0.24.11", {"center": v(148.17, 26.94) * mm, "radius": 3.18 * mm});
            skCircle(sketch, "E10.0.24.12", {"center": v(148.17, 40.41) * mm, "radius": 3.18 * mm});
            skCircle(sketch, "E10.0.24.13", {"center": v(148.17, 53.88) * mm, "radius": 3.18 * mm});
            skCircle(sketch, "E10.0.24.14", {"center": v(148.17, 67.35) * mm, "radius": 3.18 * mm});
            skCircle(sketch, "E10.0.24.15", {"center": v(148.17, 80.82) * mm, "radius": 3.18 * mm});
            skCircle(sketch, "E10.0.24.16", {"center": v(148.17, 94.3) * mm, "radius": 3.18 * mm});
            skCircle(sketch, "E10.0.24.17", {"center": v(148.17, 107.76) * mm, "radius": 3.18 * mm});
            skCircle(sketch, "E10.0.24.18", {"center": v(148.17, 121.23) * mm, "radius": 3.18 * mm});
            skCircle(sketch, "E10.0.24.19", {"center": v(148.17, 134.7) * mm, "radius": 3.18 * mm});
            skCircle(sketch, "E10.0.24.20", {"center": v(148.17, 148.17) * mm, "radius": 3.18 * mm});
            skCircle(sketch, "E10.0.24.21", {"center": v(148.17, 161.64) * mm, "radius": 3.18 * mm});
            skCircle(sketch, "E10.0.24.22", {"center": v(148.17, 175.11) * mm, "radius": 3.18 * mm});
            skCircle(sketch, "E10.0.24.23", {"center": v(148.17, 188.59) * mm, "radius": 3.18 * mm});
            skCircle(sketch, "E10.0.24.24", {"center": v(148.17, 202.06) * mm, "radius": 3.18 * mm});
            skCircle(sketch, "E11.0.3.0", {"center": v(-127.97, -114.5) * mm, "radius": 3.18 * mm});
            skCircle(sketch, "E11.0.3.1", {"center": v(-127.97, -101.03) * mm, "radius": 3.18 * mm});
            skCircle(sketch, "E11.0.3.2", {"center": v(-127.97, -87.56) * mm, "radius": 3.18 * mm});
            skCircle(sketch, "E11.0.3.3", {"center": v(-127.97, -74.09) * mm, "radius": 3.18 * mm});
            skCircle(sketch, "E11.0.3.4", {"center": v(-127.97, -60.62) * mm, "radius": 3.18 * mm});
            skCircle(sketch, "E11.0.3.5", {"center": v(-127.97, -47.15) * mm, "radius": 3.18 * mm});
            skCircle(sketch, "E11.0.3.6", {"center": v(-127.97, -33.68) * mm, "radius": 3.18 * mm});
            skCircle(sketch, "E11.0.3.7", {"center": v(-127.97, -20.2) * mm, "radius": 3.18 * mm});
            skCircle(sketch, "E11.0.3.8", {"center": v(-127.97, -6.74) * mm, "radius": 3.18 * mm});
            skCircle(sketch, "E11.0.3.9", {"center": v(-127.97, 6.74) * mm, "radius": 3.18 * mm});
            skCircle(sketch, "E11.0.3.10", {"center": v(-127.97, 20.2) * mm, "radius": 3.18 * mm});
            skCircle(sketch, "E11.0.3.11", {"center": v(-127.97, 33.68) * mm, "radius": 3.18 * mm});
            skCircle(sketch, "E11.0.3.12", {"center": v(-127.97, 47.15) * mm, "radius": 3.18 * mm});
            skCircle(sketch, "E11.0.3.13", {"center": v(-127.97, 60.62) * mm, "radius": 3.18 * mm});
            skCircle(sketch, "E11.0.3.14", {"center": v(-127.97, 74.09) * mm, "radius": 3.18 * mm});
            skCircle(sketch, "E11.0.3.15", {"center": v(-127.97, 87.56) * mm, "radius": 3.18 * mm});
            skCircle(sketch, "E11.0.3.16", {"center": v(-127.97, 101.03) * mm, "radius": 3.18 * mm});
            skCircle(sketch, "E11.0.3.17", {"center": v(-127.97, 114.5) * mm, "radius": 3.18 * mm});
            skCircle(sketch, "E11.0.3.18", {"center": v(-127.97, 127.97) * mm, "radius": 3.18 * mm});
            skCircle(sketch, "E11.0.3.19", {"center": v(-127.97, 141.44) * mm, "radius": 3.18 * mm});
            skCircle(sketch, "E11.0.3.20", {"center": v(-127.97, 154.9) * mm, "radius": 3.18 * mm});
            skCircle(sketch, "E11.0.3.21", {"center": v(-127.97, 168.38) * mm, "radius": 3.18 * mm});
            skCircle(sketch, "E11.0.3.22", {"center": v(-127.97, 181.85) * mm, "radius": 3.18 * mm});
            skCircle(sketch, "E11.0.3.23", {"center": v(-127.97, 195.32) * mm, "radius": 3.18 * mm});
            skCircle(sketch, "E11.0.3.24", {"center": v(-127.97, 208.8) * mm, "radius": 3.18 * mm});
            skCircle(sketch, "E11.0.4.0", {"center": v(-114.5, -114.5) * mm, "radius": 3.18 * mm});
            skCircle(sketch, "E11.0.4.1", {"center": v(-114.5, -101.03) * mm, "radius": 3.18 * mm});
            skCircle(sketch, "E11.0.4.2", {"center": v(-114.5, -87.56) * mm, "radius": 3.18 * mm});
            skCircle(sketch, "E11.0.4.3", {"center": v(-114.5, -74.09) * mm, "radius": 3.18 * mm});
            skCircle(sketch, "E11.0.4.4", {"center": v(-114.5, -60.62) * mm, "radius": 3.18 * mm});
            skCircle(sketch, "E11.0.4.5", {"center": v(-114.5, -47.15) * mm, "radius": 3.18 * mm});
            skCircle(sketch, "E11.0.4.6", {"center": v(-114.5, -33.68) * mm, "radius": 3.18 * mm});
            skCircle(sketch, "E11.0.4.7", {"center": v(-114.5, -20.2) * mm, "radius": 3.18 * mm});
            skCircle(sketch, "E11.0.4.8", {"center": v(-114.5, -6.74) * mm, "radius": 3.18 * mm});
            skCircle(sketch, "E11.0.4.9", {"center": v(-114.5, 6.74) * mm, "radius": 3.18 * mm});
            skCircle(sketch, "E11.0.4.10", {"center": v(-114.5, 20.2) * mm, "radius": 3.18 * mm});
            skCircle(sketch, "E11.0.4.11", {"center": v(-114.5, 33.68) * mm, "radius": 3.18 * mm});
            skCircle(sketch, "E11.0.4.12", {"center": v(-114.5, 47.15) * mm, "radius": 3.18 * mm});
            skCircle(sketch, "E11.0.4.13", {"center": v(-114.5, 60.62) * mm, "radius": 3.18 * mm});
            skCircle(sketch, "E11.0.4.14", {"center": v(-114.5, 74.09) * mm, "radius": 3.18 * mm});
            skCircle(sketch, "E11.0.4.15", {"center": v(-114.5, 87.56) * mm, "radius": 3.18 * mm});
            skCircle(sketch, "E11.0.4.16", {"center": v(-114.5, 101.03) * mm, "radius": 3.18 * mm});
            skCircle(sketch, "E11.0.4.17", {"center": v(-114.5, 114.5) * mm, "radius": 3.18 * mm});
            skCircle(sketch, "E11.0.4.18", {"center": v(-114.5, 127.97) * mm, "radius": 3.18 * mm});
            skCircle(sketch, "E11.0.4.19", {"center": v(-114.5, 141.44) * mm, "radius": 3.18 * mm});
            skCircle(sketch, "E11.0.4.20", {"center": v(-114.5, 154.9) * mm, "radius": 3.18 * mm});
            skCircle(sketch, "E11.0.4.21", {"center": v(-114.5, 168.38) * mm, "radius": 3.18 * mm});
            skCircle(sketch, "E11.0.4.22", {"center": v(-114.5, 181.85) * mm, "radius": 3.18 * mm});
            skCircle(sketch, "E11.0.4.23", {"center": v(-114.5, 195.32) * mm, "radius": 3.18 * mm});
            skCircle(sketch, "E11.0.4.24", {"center": v(-114.5, 208.8) * mm, "radius": 3.18 * mm});
            skCircle(sketch, "E11.0.5.0", {"center": v(-101.03, -114.5) * mm, "radius": 3.18 * mm});
            skCircle(sketch, "E11.0.5.1", {"center": v(-101.03, -101.03) * mm, "radius": 3.18 * mm});
            skCircle(sketch, "E11.0.5.2", {"center": v(-101.03, -87.56) * mm, "radius": 3.18 * mm});
            skCircle(sketch, "E11.0.5.3", {"center": v(-101.03, -74.09) * mm, "radius": 3.18 * mm});
            skCircle(sketch, "E11.0.5.4", {"center": v(-101.03, -60.62) * mm, "radius": 3.18 * mm});
            skCircle(sketch, "E11.0.5.5", {"center": v(-101.03, -47.15) * mm, "radius": 3.18 * mm});
            skCircle(sketch, "E11.0.5.6", {"center": v(-101.03, -33.68) * mm, "radius": 3.18 * mm});
            skCircle(sketch, "E11.0.5.7", {"center": v(-101.03, -20.2) * mm, "radius": 3.18 * mm});
            skCircle(sketch, "E11.0.5.8", {"center": v(-101.03, -6.74) * mm, "radius": 3.18 * mm});
            skCircle(sketch, "E11.0.5.9", {"center": v(-101.03, 6.74) * mm, "radius": 3.18 * mm});
            skCircle(sketch, "E11.0.5.10", {"center": v(-101.03, 20.2) * mm, "radius": 3.18 * mm});
            skCircle(sketch, "E11.0.5.11", {"center": v(-101.03, 33.68) * mm, "radius": 3.18 * mm});
            skCircle(sketch, "E11.0.5.12", {"center": v(-101.03, 47.15) * mm, "radius": 3.18 * mm});
            skCircle(sketch, "E11.0.5.13", {"center": v(-101.03, 60.62) * mm, "radius": 3.18 * mm});
            skCircle(sketch, "E11.0.5.14", {"center": v(-101.03, 74.09) * mm, "radius": 3.18 * mm});
            skCircle(sketch, "E11.0.5.15", {"center": v(-101.03, 87.56) * mm, "radius": 3.18 * mm});
            skCircle(sketch, "E11.0.5.16", {"center": v(-101.03, 101.03) * mm, "radius": 3.18 * mm});
            skCircle(sketch, "E11.0.5.17", {"center": v(-101.03, 114.5) * mm, "radius": 3.18 * mm});
            skCircle(sketch, "E11.0.5.18", {"center": v(-101.03, 127.97) * mm, "radius": 3.18 * mm});
            skCircle(sketch, "E11.0.5.19", {"center": v(-101.03, 141.44) * mm, "radius": 3.18 * mm});
            skCircle(sketch, "E11.0.5.20", {"center": v(-101.03, 154.9) * mm, "radius": 3.18 * mm});
            skCircle(sketch, "E11.0.5.21", {"center": v(-101.03, 168.38) * mm, "radius": 3.18 * mm});
            skCircle(sketch, "E11.0.5.22", {"center": v(-101.03, 181.85) * mm, "radius": 3.18 * mm});
            skCircle(sketch, "E11.0.5.23", {"center": v(-101.03, 195.32) * mm, "radius": 3.18 * mm});
            skCircle(sketch, "E11.0.5.24", {"center": v(-101.03, 208.8) * mm, "radius": 3.18 * mm});
            skCircle(sketch, "E11.0.6.0", {"center": v(-87.56, -114.5) * mm, "radius": 3.18 * mm});
            skCircle(sketch, "E11.0.6.1", {"center": v(-87.56, -101.03) * mm, "radius": 3.18 * mm});
            skCircle(sketch, "E11.0.6.2", {"center": v(-87.56, -87.56) * mm, "radius": 3.18 * mm});
            skCircle(sketch, "E11.0.6.3", {"center": v(-87.56, -74.09) * mm, "radius": 3.18 * mm});
            skCircle(sketch, "E11.0.6.4", {"center": v(-87.56, -60.62) * mm, "radius": 3.18 * mm});
            skCircle(sketch, "E11.0.6.5", {"center": v(-87.56, -47.15) * mm, "radius": 3.18 * mm});
            skCircle(sketch, "E11.0.6.6", {"center": v(-87.56, -33.68) * mm, "radius": 3.18 * mm});
            skCircle(sketch, "E11.0.6.7", {"center": v(-87.56, -20.2) * mm, "radius": 3.18 * mm});
            skCircle(sketch, "E11.0.6.8", {"center": v(-87.56, -6.74) * mm, "radius": 3.18 * mm});
            skCircle(sketch, "E11.0.6.9", {"center": v(-87.56, 6.74) * mm, "radius": 3.18 * mm});
            skCircle(sketch, "E11.0.6.10", {"center": v(-87.56, 20.2) * mm, "radius": 3.18 * mm});
            skCircle(sketch, "E11.0.6.11", {"center": v(-87.56, 33.68) * mm, "radius": 3.18 * mm});
            skCircle(sketch, "E11.0.6.12", {"center": v(-87.56, 47.15) * mm, "radius": 3.18 * mm});
            skCircle(sketch, "E11.0.6.13", {"center": v(-87.56, 60.62) * mm, "radius": 3.18 * mm});
            skCircle(sketch, "E11.0.6.14", {"center": v(-87.56, 74.09) * mm, "radius": 3.18 * mm});
            skCircle(sketch, "E11.0.6.15", {"center": v(-87.56, 87.56) * mm, "radius": 3.18 * mm});
            skCircle(sketch, "E11.0.6.16", {"center": v(-87.56, 101.03) * mm, "radius": 3.18 * mm});
            skCircle(sketch, "E11.0.6.17", {"center": v(-87.56, 114.5) * mm, "radius": 3.18 * mm});
            skCircle(sketch, "E11.0.6.18", {"center": v(-87.56, 127.97) * mm, "radius": 3.18 * mm});
            skCircle(sketch, "E11.0.6.19", {"center": v(-87.56, 141.44) * mm, "radius": 3.18 * mm});
            skCircle(sketch, "E11.0.6.20", {"center": v(-87.56, 154.9) * mm, "radius": 3.18 * mm});
            skCircle(sketch, "E11.0.6.21", {"center": v(-87.56, 168.38) * mm, "radius": 3.18 * mm});
            skCircle(sketch, "E11.0.6.22", {"center": v(-87.56, 181.85) * mm, "radius": 3.18 * mm});
            skCircle(sketch, "E11.0.6.23", {"center": v(-87.56, 195.32) * mm, "radius": 3.18 * mm});
            skCircle(sketch, "E11.0.6.24", {"center": v(-87.56, 208.8) * mm, "radius": 3.18 * mm});
            skCircle(sketch, "E11.0.7.0", {"center": v(-74.09, -114.5) * mm, "radius": 3.18 * mm});
            skCircle(sketch, "E11.0.7.1", {"center": v(-74.09, -101.03) * mm, "radius": 3.18 * mm});
            skCircle(sketch, "E11.0.7.2", {"center": v(-74.09, -87.56) * mm, "radius": 3.18 * mm});
            skCircle(sketch, "E11.0.7.3", {"center": v(-74.09, -74.09) * mm, "radius": 3.18 * mm});
            skCircle(sketch, "E11.0.7.4", {"center": v(-74.09, -60.62) * mm, "radius": 3.18 * mm});
            skCircle(sketch, "E11.0.7.5", {"center": v(-74.09, -47.15) * mm, "radius": 3.18 * mm});
            skCircle(sketch, "E11.0.7.6", {"center": v(-74.09, -33.68) * mm, "radius": 3.18 * mm});
            skCircle(sketch, "E11.0.7.7", {"center": v(-74.09, -20.2) * mm, "radius": 3.18 * mm});
            skCircle(sketch, "E11.0.7.8", {"center": v(-74.09, -6.74) * mm, "radius": 3.18 * mm});
            skCircle(sketch, "E11.0.7.9", {"center": v(-74.09, 6.74) * mm, "radius": 3.18 * mm});
            skCircle(sketch, "E11.0.7.10", {"center": v(-74.09, 20.2) * mm, "radius": 3.18 * mm});
            skCircle(sketch, "E11.0.7.11", {"center": v(-74.09, 33.68) * mm, "radius": 3.18 * mm});
            skCircle(sketch, "E11.0.7.12", {"center": v(-74.09, 47.15) * mm, "radius": 3.18 * mm});
            skCircle(sketch, "E11.0.7.13", {"center": v(-74.09, 60.62) * mm, "radius": 3.18 * mm});
            skCircle(sketch, "E11.0.7.14", {"center": v(-74.09, 74.09) * mm, "radius": 3.18 * mm});
            skCircle(sketch, "E11.0.7.15", {"center": v(-74.09, 87.56) * mm, "radius": 3.18 * mm});
            skCircle(sketch, "E11.0.7.16", {"center": v(-74.09, 101.03) * mm, "radius": 3.18 * mm});
            skCircle(sketch, "E11.0.7.17", {"center": v(-74.09, 114.5) * mm, "radius": 3.18 * mm});
            skCircle(sketch, "E11.0.7.18", {"center": v(-74.09, 127.97) * mm, "radius": 3.18 * mm});
            skCircle(sketch, "E11.0.7.19", {"center": v(-74.09, 141.44) * mm, "radius": 3.18 * mm});
            skCircle(sketch, "E11.0.7.20", {"center": v(-74.09, 154.9) * mm, "radius": 3.18 * mm});
            skCircle(sketch, "E11.0.7.21", {"center": v(-74.09, 168.38) * mm, "radius": 3.18 * mm});
            skCircle(sketch, "E11.0.7.22", {"center": v(-74.09, 181.85) * mm, "radius": 3.18 * mm});
            skCircle(sketch, "E11.0.7.23", {"center": v(-74.09, 195.32) * mm, "radius": 3.18 * mm});
            skCircle(sketch, "E11.0.7.24", {"center": v(-74.09, 208.8) * mm, "radius": 3.18 * mm});
            skCircle(sketch, "E11.0.8.0", {"center": v(-60.62, -114.5) * mm, "radius": 3.18 * mm});
            skCircle(sketch, "E11.0.8.1", {"center": v(-60.62, -101.03) * mm, "radius": 3.18 * mm});
            skCircle(sketch, "E11.0.8.2", {"center": v(-60.62, -87.56) * mm, "radius": 3.18 * mm});
            skCircle(sketch, "E11.0.8.3", {"center": v(-60.62, -74.09) * mm, "radius": 3.18 * mm});
            skCircle(sketch, "E11.0.8.4", {"center": v(-60.62, -60.62) * mm, "radius": 3.18 * mm});
            skCircle(sketch, "E11.0.8.5", {"center": v(-60.62, -47.15) * mm, "radius": 3.18 * mm});
            skCircle(sketch, "E11.0.8.6", {"center": v(-60.62, -33.68) * mm, "radius": 3.18 * mm});
            skCircle(sketch, "E11.0.8.7", {"center": v(-60.62, -20.2) * mm, "radius": 3.18 * mm});
            skCircle(sketch, "E11.0.8.8", {"center": v(-60.62, -6.74) * mm, "radius": 3.18 * mm});
            skCircle(sketch, "E11.0.8.9", {"center": v(-60.62, 6.74) * mm, "radius": 3.18 * mm});
            skCircle(sketch, "E11.0.8.10", {"center": v(-60.62, 20.2) * mm, "radius": 3.18 * mm});
            skCircle(sketch, "E11.0.8.11", {"center": v(-60.62, 33.68) * mm, "radius": 3.18 * mm});
            skCircle(sketch, "E11.0.8.12", {"center": v(-60.62, 47.15) * mm, "radius": 3.18 * mm});
            skCircle(sketch, "E11.0.8.13", {"center": v(-60.62, 60.62) * mm, "radius": 3.18 * mm});
            skCircle(sketch, "E11.0.8.14", {"center": v(-60.62, 74.09) * mm, "radius": 3.18 * mm});
            skCircle(sketch, "E11.0.8.15", {"center": v(-60.62, 87.56) * mm, "radius": 3.18 * mm});
            skCircle(sketch, "E11.0.8.16", {"center": v(-60.62, 101.03) * mm, "radius": 3.18 * mm});
            skCircle(sketch, "E11.0.8.17", {"center": v(-60.62, 114.5) * mm, "radius": 3.18 * mm});
            skCircle(sketch, "E11.0.8.18", {"center": v(-60.62, 127.97) * mm, "radius": 3.18 * mm});
            skCircle(sketch, "E11.0.8.19", {"center": v(-60.62, 141.44) * mm, "radius": 3.18 * mm});
            skCircle(sketch, "E11.0.8.20", {"center": v(-60.62, 154.9) * mm, "radius": 3.18 * mm});
            skCircle(sketch, "E11.0.8.21", {"center": v(-60.62, 168.38) * mm, "radius": 3.18 * mm});
            skCircle(sketch, "E11.0.8.22", {"center": v(-60.62, 181.85) * mm, "radius": 3.18 * mm});
            skCircle(sketch, "E11.0.8.23", {"center": v(-60.62, 195.32) * mm, "radius": 3.18 * mm});
            skCircle(sketch, "E11.0.8.24", {"center": v(-60.62, 208.8) * mm, "radius": 3.18 * mm});
            skCircle(sketch, "E11.0.9.0", {"center": v(-47.15, -114.5) * mm, "radius": 3.18 * mm});
            skCircle(sketch, "E11.0.9.1", {"center": v(-47.15, -101.03) * mm, "radius": 3.18 * mm});
            skCircle(sketch, "E11.0.9.2", {"center": v(-47.15, -87.56) * mm, "radius": 3.18 * mm});
            skCircle(sketch, "E11.0.9.3", {"center": v(-47.15, -74.09) * mm, "radius": 3.18 * mm});
            skCircle(sketch, "E11.0.9.4", {"center": v(-47.15, -60.62) * mm, "radius": 3.18 * mm});
            skCircle(sketch, "E11.0.9.5", {"center": v(-47.15, -47.15) * mm, "radius": 3.18 * mm});
            skCircle(sketch, "E11.0.9.6", {"center": v(-47.15, -33.68) * mm, "radius": 3.18 * mm});
            skCircle(sketch, "E11.0.9.7", {"center": v(-47.15, -20.2) * mm, "radius": 3.18 * mm});
            skCircle(sketch, "E11.0.9.8", {"center": v(-47.15, -6.74) * mm, "radius": 3.18 * mm});
            skCircle(sketch, "E11.0.9.9", {"center": v(-47.15, 6.74) * mm, "radius": 3.18 * mm});
            skCircle(sketch, "E11.0.9.10", {"center": v(-47.15, 20.2) * mm, "radius": 3.18 * mm});
            skCircle(sketch, "E11.0.9.11", {"center": v(-47.15, 33.68) * mm, "radius": 3.18 * mm});
            skCircle(sketch, "E11.0.9.12", {"center": v(-47.15, 47.15) * mm, "radius": 3.18 * mm});
            skCircle(sketch, "E11.0.9.13", {"center": v(-47.15, 60.62) * mm, "radius": 3.18 * mm});
            skCircle(sketch, "E11.0.9.14", {"center": v(-47.15, 74.09) * mm, "radius": 3.18 * mm});
            skCircle(sketch, "E11.0.9.15", {"center": v(-47.15, 87.56) * mm, "radius": 3.18 * mm});
            skCircle(sketch, "E11.0.9.16", {"center": v(-47.15, 101.03) * mm, "radius": 3.18 * mm});
            skCircle(sketch, "E11.0.9.17", {"center": v(-47.15, 114.5) * mm, "radius": 3.18 * mm});
            skCircle(sketch, "E11.0.9.18", {"center": v(-47.15, 127.97) * mm, "radius": 3.18 * mm});
            skCircle(sketch, "E11.0.9.19", {"center": v(-47.15, 141.44) * mm, "radius": 3.18 * mm});
            skCircle(sketch, "E11.0.9.20", {"center": v(-47.15, 154.9) * mm, "radius": 3.18 * mm});
            skCircle(sketch, "E11.0.9.21", {"center": v(-47.15, 168.38) * mm, "radius": 3.18 * mm});
            skCircle(sketch, "E11.0.9.22", {"center": v(-47.15, 181.85) * mm, "radius": 3.18 * mm});
            skCircle(sketch, "E11.0.9.23", {"center": v(-47.15, 195.32) * mm, "radius": 3.18 * mm});
            skCircle(sketch, "E11.0.9.24", {"center": v(-47.15, 208.8) * mm, "radius": 3.18 * mm});
            skCircle(sketch, "E11.0.10.0", {"center": v(-33.68, -114.5) * mm, "radius": 3.18 * mm});
            skCircle(sketch, "E11.0.10.1", {"center": v(-33.68, -101.03) * mm, "radius": 3.18 * mm});
            skCircle(sketch, "E11.0.10.2", {"center": v(-33.68, -87.56) * mm, "radius": 3.18 * mm});
            skCircle(sketch, "E11.0.10.3", {"center": v(-33.68, -74.09) * mm, "radius": 3.18 * mm});
            skCircle(sketch, "E11.0.10.4", {"center": v(-33.68, -60.62) * mm, "radius": 3.18 * mm});
            skCircle(sketch, "E11.0.10.5", {"center": v(-33.68, -47.15) * mm, "radius": 3.18 * mm});
            skCircle(sketch, "E11.0.10.6", {"center": v(-33.68, -33.68) * mm, "radius": 3.18 * mm});
            skCircle(sketch, "E11.0.10.7", {"center": v(-33.68, -20.2) * mm, "radius": 3.18 * mm});
            skCircle(sketch, "E11.0.10.8", {"center": v(-33.68, -6.74) * mm, "radius": 3.18 * mm});
            skCircle(sketch, "E11.0.10.9", {"center": v(-33.68, 6.74) * mm, "radius": 3.18 * mm});
            skCircle(sketch, "E11.0.10.10", {"center": v(-33.68, 20.2) * mm, "radius": 3.18 * mm});
            skCircle(sketch, "E11.0.10.11", {"center": v(-33.68, 33.68) * mm, "radius": 3.18 * mm});
            skCircle(sketch, "E11.0.10.12", {"center": v(-33.68, 47.15) * mm, "radius": 3.18 * mm});
            skCircle(sketch, "E11.0.10.13", {"center": v(-33.68, 60.62) * mm, "radius": 3.18 * mm});
            skCircle(sketch, "E11.0.10.14", {"center": v(-33.68, 74.09) * mm, "radius": 3.18 * mm});
            skCircle(sketch, "E11.0.10.15", {"center": v(-33.68, 87.56) * mm, "radius": 3.18 * mm});
            skCircle(sketch, "E11.0.10.16", {"center": v(-33.68, 101.03) * mm, "radius": 3.18 * mm});
            skCircle(sketch, "E11.0.10.17", {"center": v(-33.68, 114.5) * mm, "radius": 3.18 * mm});
            skCircle(sketch, "E11.0.10.18", {"center": v(-33.68, 127.97) * mm, "radius": 3.18 * mm});
            skCircle(sketch, "E11.0.10.19", {"center": v(-33.68, 141.44) * mm, "radius": 3.18 * mm});
            skCircle(sketch, "E11.0.10.20", {"center": v(-33.68, 154.9) * mm, "radius": 3.18 * mm});
            skCircle(sketch, "E11.0.10.21", {"center": v(-33.68, 168.38) * mm, "radius": 3.18 * mm});
            skCircle(sketch, "E11.0.10.22", {"center": v(-33.68, 181.85) * mm, "radius": 3.18 * mm});
            skCircle(sketch, "E11.0.10.23", {"center": v(-33.68, 195.32) * mm, "radius": 3.18 * mm});
            skCircle(sketch, "E11.0.10.24", {"center": v(-33.68, 208.8) * mm, "radius": 3.18 * mm});
            skCircle(sketch, "E11.0.11.0", {"center": v(-20.2, -114.5) * mm, "radius": 3.18 * mm});
            skCircle(sketch, "E11.0.11.1", {"center": v(-20.2, -101.03) * mm, "radius": 3.18 * mm});
            skCircle(sketch, "E11.0.11.2", {"center": v(-20.2, -87.56) * mm, "radius": 3.18 * mm});
            skCircle(sketch, "E11.0.11.3", {"center": v(-20.2, -74.09) * mm, "radius": 3.18 * mm});
            skCircle(sketch, "E11.0.11.4", {"center": v(-20.2, -60.62) * mm, "radius": 3.18 * mm});
            skCircle(sketch, "E11.0.11.5", {"center": v(-20.2, -47.15) * mm, "radius": 3.18 * mm});
            skCircle(sketch, "E11.0.11.6", {"center": v(-20.2, -33.68) * mm, "radius": 3.18 * mm});
            skCircle(sketch, "E11.0.11.7", {"center": v(-20.2, -20.2) * mm, "radius": 3.18 * mm});
            skCircle(sketch, "E11.0.11.8", {"center": v(-20.2, -6.74) * mm, "radius": 3.18 * mm});
            skCircle(sketch, "E11.0.11.9", {"center": v(-20.2, 6.74) * mm, "radius": 3.18 * mm});
            skCircle(sketch, "E11.0.11.10", {"center": v(-20.2, 20.2) * mm, "radius": 3.18 * mm});
            skCircle(sketch, "E11.0.11.11", {"center": v(-20.2, 33.68) * mm, "radius": 3.18 * mm});
            skCircle(sketch, "E11.0.11.12", {"center": v(-20.2, 47.15) * mm, "radius": 3.18 * mm});
            skCircle(sketch, "E11.0.11.13", {"center": v(-20.2, 60.62) * mm, "radius": 3.18 * mm});
            skCircle(sketch, "E11.0.11.14", {"center": v(-20.2, 74.09) * mm, "radius": 3.18 * mm});
            skCircle(sketch, "E11.0.11.15", {"center": v(-20.2, 87.56) * mm, "radius": 3.18 * mm});
            skCircle(sketch, "E11.0.11.16", {"center": v(-20.2, 101.03) * mm, "radius": 3.18 * mm});
            skCircle(sketch, "E11.0.11.17", {"center": v(-20.2, 114.5) * mm, "radius": 3.18 * mm});
            skCircle(sketch, "E11.0.11.18", {"center": v(-20.2, 127.97) * mm, "radius": 3.18 * mm});
            skCircle(sketch, "E11.0.11.19", {"center": v(-20.2, 141.44) * mm, "radius": 3.18 * mm});
            skCircle(sketch, "E11.0.11.20", {"center": v(-20.2, 154.9) * mm, "radius": 3.18 * mm});
            skCircle(sketch, "E11.0.11.21", {"center": v(-20.2, 168.38) * mm, "radius": 3.18 * mm});
            skCircle(sketch, "E11.0.11.22", {"center": v(-20.2, 181.85) * mm, "radius": 3.18 * mm});
            skCircle(sketch, "E11.0.11.23", {"center": v(-20.2, 195.32) * mm, "radius": 3.18 * mm});
            skCircle(sketch, "E11.0.11.24", {"center": v(-20.2, 208.8) * mm, "radius": 3.18 * mm});
            skCircle(sketch, "E11.0.12.0", {"center": v(-6.74, -114.5) * mm, "radius": 3.18 * mm});
            skCircle(sketch, "E11.0.12.1", {"center": v(-6.74, -101.03) * mm, "radius": 3.18 * mm});
            skCircle(sketch, "E11.0.12.2", {"center": v(-6.74, -87.56) * mm, "radius": 3.18 * mm});
            skCircle(sketch, "E11.0.12.3", {"center": v(-6.74, -74.09) * mm, "radius": 3.18 * mm});
            skCircle(sketch, "E11.0.12.4", {"center": v(-6.74, -60.62) * mm, "radius": 3.18 * mm});
            skCircle(sketch, "E11.0.12.5", {"center": v(-6.74, -47.15) * mm, "radius": 3.18 * mm});
            skCircle(sketch, "E11.0.12.6", {"center": v(-6.74, -33.68) * mm, "radius": 3.18 * mm});
            skCircle(sketch, "E11.0.12.7", {"center": v(-6.74, -20.2) * mm, "radius": 3.18 * mm});
            skCircle(sketch, "E11.0.12.8", {"center": v(-6.74, -6.74) * mm, "radius": 3.18 * mm});
            skCircle(sketch, "E11.0.12.9", {"center": v(-6.74, 6.74) * mm, "radius": 3.18 * mm});
            skCircle(sketch, "E11.0.12.10", {"center": v(-6.74, 20.2) * mm, "radius": 3.18 * mm});
            skCircle(sketch, "E11.0.12.11", {"center": v(-6.74, 33.68) * mm, "radius": 3.18 * mm});
            skCircle(sketch, "E11.0.12.12", {"center": v(-6.74, 47.15) * mm, "radius": 3.18 * mm});
            skCircle(sketch, "E11.0.12.13", {"center": v(-6.74, 60.62) * mm, "radius": 3.18 * mm});
            skCircle(sketch, "E11.0.12.14", {"center": v(-6.74, 74.09) * mm, "radius": 3.18 * mm});
            skCircle(sketch, "E11.0.12.15", {"center": v(-6.74, 87.56) * mm, "radius": 3.18 * mm});
            skCircle(sketch, "E11.0.12.16", {"center": v(-6.74, 101.03) * mm, "radius": 3.18 * mm});
            skCircle(sketch, "E11.0.12.17", {"center": v(-6.74, 114.5) * mm, "radius": 3.18 * mm});
            skCircle(sketch, "E11.0.12.18", {"center": v(-6.74, 127.97) * mm, "radius": 3.18 * mm});
            skCircle(sketch, "E11.0.12.19", {"center": v(-6.74, 141.44) * mm, "radius": 3.18 * mm});
            skCircle(sketch, "E11.0.12.20", {"center": v(-6.74, 154.9) * mm, "radius": 3.18 * mm});
            skCircle(sketch, "E11.0.12.21", {"center": v(-6.74, 168.38) * mm, "radius": 3.18 * mm});
            skCircle(sketch, "E11.0.12.22", {"center": v(-6.74, 181.85) * mm, "radius": 3.18 * mm});
            skCircle(sketch, "E11.0.12.23", {"center": v(-6.74, 195.32) * mm, "radius": 3.18 * mm});
            skCircle(sketch, "E11.0.12.24", {"center": v(-6.74, 208.8) * mm, "radius": 3.18 * mm});
            skCircle(sketch, "E11.0.13.0", {"center": v(6.74, -114.5) * mm, "radius": 3.18 * mm});
            skCircle(sketch, "E11.0.13.1", {"center": v(6.74, -101.03) * mm, "radius": 3.18 * mm});
            skCircle(sketch, "E11.0.13.2", {"center": v(6.74, -87.56) * mm, "radius": 3.18 * mm});
            skCircle(sketch, "E11.0.13.3", {"center": v(6.74, -74.09) * mm, "radius": 3.18 * mm});
            skCircle(sketch, "E11.0.13.4", {"center": v(6.74, -60.62) * mm, "radius": 3.18 * mm});
            skCircle(sketch, "E11.0.13.5", {"center": v(6.74, -47.15) * mm, "radius": 3.18 * mm});
            skCircle(sketch, "E11.0.13.6", {"center": v(6.74, -33.68) * mm, "radius": 3.18 * mm});
            skCircle(sketch, "E11.0.13.7", {"center": v(6.74, -20.2) * mm, "radius": 3.18 * mm});
            skCircle(sketch, "E11.0.13.8", {"center": v(6.74, -6.74) * mm, "radius": 3.18 * mm});
            skCircle(sketch, "E11.0.13.9", {"center": v(6.74, 6.74) * mm, "radius": 3.18 * mm});
            skCircle(sketch, "E11.0.13.10", {"center": v(6.74, 20.2) * mm, "radius": 3.18 * mm});
            skCircle(sketch, "E11.0.13.11", {"center": v(6.74, 33.68) * mm, "radius": 3.18 * mm});
            skCircle(sketch, "E11.0.13.12", {"center": v(6.74, 47.15) * mm, "radius": 3.18 * mm});
            skCircle(sketch, "E11.0.13.13", {"center": v(6.74, 60.62) * mm, "radius": 3.18 * mm});
            skCircle(sketch, "E11.0.13.14", {"center": v(6.74, 74.09) * mm, "radius": 3.18 * mm});
            skCircle(sketch, "E11.0.13.15", {"center": v(6.74, 87.56) * mm, "radius": 3.18 * mm});
            skCircle(sketch, "E11.0.13.16", {"center": v(6.74, 101.03) * mm, "radius": 3.18 * mm});
            skCircle(sketch, "E11.0.13.17", {"center": v(6.74, 114.5) * mm, "radius": 3.18 * mm});
            skCircle(sketch, "E11.0.13.18", {"center": v(6.74, 127.97) * mm, "radius": 3.18 * mm});
            skCircle(sketch, "E11.0.13.19", {"center": v(6.74, 141.44) * mm, "radius": 3.18 * mm});
            skCircle(sketch, "E11.0.13.20", {"center": v(6.74, 154.9) * mm, "radius": 3.18 * mm});
            skCircle(sketch, "E11.0.13.21", {"center": v(6.74, 168.38) * mm, "radius": 3.18 * mm});
            skCircle(sketch, "E11.0.13.22", {"center": v(6.74, 181.85) * mm, "radius": 3.18 * mm});
            skCircle(sketch, "E11.0.13.23", {"center": v(6.74, 195.32) * mm, "radius": 3.18 * mm});
            skCircle(sketch, "E11.0.13.24", {"center": v(6.74, 208.8) * mm, "radius": 3.18 * mm});
            skCircle(sketch, "E11.0.14.0", {"center": v(20.2, -114.5) * mm, "radius": 3.18 * mm});
            skCircle(sketch, "E11.0.14.1", {"center": v(20.2, -101.03) * mm, "radius": 3.18 * mm});
            skCircle(sketch, "E11.0.14.2", {"center": v(20.2, -87.56) * mm, "radius": 3.18 * mm});
            skCircle(sketch, "E11.0.14.3", {"center": v(20.2, -74.09) * mm, "radius": 3.18 * mm});
            skCircle(sketch, "E11.0.14.4", {"center": v(20.2, -60.62) * mm, "radius": 3.18 * mm});
            skCircle(sketch, "E11.0.14.5", {"center": v(20.2, -47.15) * mm, "radius": 3.18 * mm});
            skCircle(sketch, "E11.0.14.6", {"center": v(20.2, -33.68) * mm, "radius": 3.18 * mm});
            skCircle(sketch, "E11.0.14.7", {"center": v(20.2, -20.2) * mm, "radius": 3.18 * mm});
            skCircle(sketch, "E11.0.14.8", {"center": v(20.2, -6.74) * mm, "radius": 3.18 * mm});
            skCircle(sketch, "E11.0.14.9", {"center": v(20.2, 6.74) * mm, "radius": 3.18 * mm});
            skCircle(sketch, "E11.0.14.10", {"center": v(20.2, 20.2) * mm, "radius": 3.18 * mm});
            skCircle(sketch, "E11.0.14.11", {"center": v(20.2, 33.68) * mm, "radius": 3.18 * mm});
            skCircle(sketch, "E11.0.14.12", {"center": v(20.2, 47.15) * mm, "radius": 3.18 * mm});
            skCircle(sketch, "E11.0.14.13", {"center": v(20.2, 60.62) * mm, "radius": 3.18 * mm});
            skCircle(sketch, "E11.0.14.14", {"center": v(20.2, 74.09) * mm, "radius": 3.18 * mm});
            skCircle(sketch, "E11.0.14.15", {"center": v(20.2, 87.56) * mm, "radius": 3.18 * mm});
            skCircle(sketch, "E11.0.14.16", {"center": v(20.2, 101.03) * mm, "radius": 3.18 * mm});
            skCircle(sketch, "E11.0.14.17", {"center": v(20.2, 114.5) * mm, "radius": 3.18 * mm});
            skCircle(sketch, "E11.0.14.18", {"center": v(20.2, 127.97) * mm, "radius": 3.18 * mm});
            skCircle(sketch, "E11.0.14.19", {"center": v(20.2, 141.44) * mm, "radius": 3.18 * mm});
            skCircle(sketch, "E11.0.14.20", {"center": v(20.2, 154.9) * mm, "radius": 3.18 * mm});
            skCircle(sketch, "E11.0.14.21", {"center": v(20.2, 168.38) * mm, "radius": 3.18 * mm});
            skCircle(sketch, "E11.0.14.22", {"center": v(20.2, 181.85) * mm, "radius": 3.18 * mm});
            skCircle(sketch, "E11.0.14.23", {"center": v(20.2, 195.32) * mm, "radius": 3.18 * mm});
            skCircle(sketch, "E11.0.14.24", {"center": v(20.2, 208.8) * mm, "radius": 3.18 * mm});
            skCircle(sketch, "E11.0.15.0", {"center": v(33.68, -114.5) * mm, "radius": 3.18 * mm});
            skCircle(sketch, "E11.0.15.1", {"center": v(33.68, -101.03) * mm, "radius": 3.18 * mm});
            skCircle(sketch, "E11.0.15.2", {"center": v(33.68, -87.56) * mm, "radius": 3.18 * mm});
            skCircle(sketch, "E11.0.15.3", {"center": v(33.68, -74.09) * mm, "radius": 3.18 * mm});
            skCircle(sketch, "E11.0.15.4", {"center": v(33.68, -60.62) * mm, "radius": 3.18 * mm});
            skCircle(sketch, "E11.0.15.5", {"center": v(33.68, -47.15) * mm, "radius": 3.18 * mm});
            skCircle(sketch, "E11.0.15.6", {"center": v(33.68, -33.68) * mm, "radius": 3.18 * mm});
            skCircle(sketch, "E11.0.15.7", {"center": v(33.68, -20.2) * mm, "radius": 3.18 * mm});
            skCircle(sketch, "E11.0.15.8", {"center": v(33.68, -6.74) * mm, "radius": 3.18 * mm});
            skCircle(sketch, "E11.0.15.9", {"center": v(33.68, 6.74) * mm, "radius": 3.18 * mm});
            skCircle(sketch, "E11.0.15.10", {"center": v(33.68, 20.2) * mm, "radius": 3.18 * mm});
            skCircle(sketch, "E11.0.15.11", {"center": v(33.68, 33.68) * mm, "radius": 3.18 * mm});
            skCircle(sketch, "E11.0.15.12", {"center": v(33.68, 47.15) * mm, "radius": 3.18 * mm});
            skCircle(sketch, "E11.0.15.13", {"center": v(33.68, 60.62) * mm, "radius": 3.18 * mm});
            skCircle(sketch, "E11.0.15.14", {"center": v(33.68, 74.09) * mm, "radius": 3.18 * mm});
            skCircle(sketch, "E11.0.15.15", {"center": v(33.68, 87.56) * mm, "radius": 3.18 * mm});
            skCircle(sketch, "E11.0.15.16", {"center": v(33.68, 101.03) * mm, "radius": 3.18 * mm});
            skCircle(sketch, "E11.0.15.17", {"center": v(33.68, 114.5) * mm, "radius": 3.18 * mm});
            skCircle(sketch, "E11.0.15.18", {"center": v(33.68, 127.97) * mm, "radius": 3.18 * mm});
            skCircle(sketch, "E11.0.15.19", {"center": v(33.68, 141.44) * mm, "radius": 3.18 * mm});
            skCircle(sketch, "E11.0.15.20", {"center": v(33.68, 154.9) * mm, "radius": 3.18 * mm});
            skCircle(sketch, "E11.0.15.21", {"center": v(33.68, 168.38) * mm, "radius": 3.18 * mm});
            skCircle(sketch, "E11.0.15.22", {"center": v(33.68, 181.85) * mm, "radius": 3.18 * mm});
            skCircle(sketch, "E11.0.15.23", {"center": v(33.68, 195.32) * mm, "radius": 3.18 * mm});
            skCircle(sketch, "E11.0.15.24", {"center": v(33.68, 208.8) * mm, "radius": 3.18 * mm});
            skCircle(sketch, "E11.0.16.0", {"center": v(47.15, -114.5) * mm, "radius": 3.18 * mm});
            skCircle(sketch, "E11.0.16.1", {"center": v(47.15, -101.03) * mm, "radius": 3.18 * mm});
            skCircle(sketch, "E11.0.16.2", {"center": v(47.15, -87.56) * mm, "radius": 3.18 * mm});
            skCircle(sketch, "E11.0.16.3", {"center": v(47.15, -74.09) * mm, "radius": 3.18 * mm});
            skCircle(sketch, "E11.0.16.4", {"center": v(47.15, -60.62) * mm, "radius": 3.18 * mm});
            skCircle(sketch, "E11.0.16.5", {"center": v(47.15, -47.15) * mm, "radius": 3.18 * mm});
            skCircle(sketch, "E11.0.16.6", {"center": v(47.15, -33.68) * mm, "radius": 3.18 * mm});
            skCircle(sketch, "E11.0.16.7", {"center": v(47.15, -20.2) * mm, "radius": 3.18 * mm});
            skCircle(sketch, "E11.0.16.8", {"center": v(47.15, -6.74) * mm, "radius": 3.18 * mm});
            skCircle(sketch, "E11.0.16.9", {"center": v(47.15, 6.74) * mm, "radius": 3.18 * mm});
            skCircle(sketch, "E11.0.16.10", {"center": v(47.15, 20.2) * mm, "radius": 3.18 * mm});
            skCircle(sketch, "E11.0.16.11", {"center": v(47.15, 33.68) * mm, "radius": 3.18 * mm});
            skCircle(sketch, "E11.0.16.12", {"center": v(47.15, 47.15) * mm, "radius": 3.18 * mm});
            skCircle(sketch, "E11.0.16.13", {"center": v(47.15, 60.62) * mm, "radius": 3.18 * mm});
            skCircle(sketch, "E11.0.16.14", {"center": v(47.15, 74.09) * mm, "radius": 3.18 * mm});
            skCircle(sketch, "E11.0.16.15", {"center": v(47.15, 87.56) * mm, "radius": 3.18 * mm});
            skCircle(sketch, "E11.0.16.16", {"center": v(47.15, 101.03) * mm, "radius": 3.18 * mm});
            skCircle(sketch, "E11.0.16.17", {"center": v(47.15, 114.5) * mm, "radius": 3.18 * mm});
            skCircle(sketch, "E11.0.16.18", {"center": v(47.15, 127.97) * mm, "radius": 3.18 * mm});
            skCircle(sketch, "E11.0.16.19", {"center": v(47.15, 141.44) * mm, "radius": 3.18 * mm});
            skCircle(sketch, "E11.0.16.20", {"center": v(47.15, 154.9) * mm, "radius": 3.18 * mm});
            skCircle(sketch, "E11.0.16.21", {"center": v(47.15, 168.38) * mm, "radius": 3.18 * mm});
            skCircle(sketch, "E11.0.16.22", {"center": v(47.15, 181.85) * mm, "radius": 3.18 * mm});
            skCircle(sketch, "E11.0.16.23", {"center": v(47.15, 195.32) * mm, "radius": 3.18 * mm});
            skCircle(sketch, "E11.0.16.24", {"center": v(47.15, 208.8) * mm, "radius": 3.18 * mm});
            skCircle(sketch, "E11.0.17.0", {"center": v(60.62, -114.5) * mm, "radius": 3.18 * mm});
            skCircle(sketch, "E11.0.17.1", {"center": v(60.62, -101.03) * mm, "radius": 3.18 * mm});
            skCircle(sketch, "E11.0.17.2", {"center": v(60.62, -87.56) * mm, "radius": 3.18 * mm});
            skCircle(sketch, "E11.0.17.3", {"center": v(60.62, -74.09) * mm, "radius": 3.18 * mm});
            skCircle(sketch, "E11.0.17.4", {"center": v(60.62, -60.62) * mm, "radius": 3.18 * mm});
            skCircle(sketch, "E11.0.17.5", {"center": v(60.62, -47.15) * mm, "radius": 3.18 * mm});
            skCircle(sketch, "E11.0.17.6", {"center": v(60.62, -33.68) * mm, "radius": 3.18 * mm});
            skCircle(sketch, "E11.0.17.7", {"center": v(60.62, -20.2) * mm, "radius": 3.18 * mm});
            skCircle(sketch, "E11.0.17.8", {"center": v(60.62, -6.74) * mm, "radius": 3.18 * mm});
            skCircle(sketch, "E11.0.17.9", {"center": v(60.62, 6.74) * mm, "radius": 3.18 * mm});
            skCircle(sketch, "E11.0.17.10", {"center": v(60.62, 20.2) * mm, "radius": 3.18 * mm});
            skCircle(sketch, "E11.0.17.11", {"center": v(60.62, 33.68) * mm, "radius": 3.18 * mm});
            skCircle(sketch, "E11.0.17.12", {"center": v(60.62, 47.15) * mm, "radius": 3.18 * mm});
            skCircle(sketch, "E11.0.17.13", {"center": v(60.62, 60.62) * mm, "radius": 3.18 * mm});
            skCircle(sketch, "E11.0.17.14", {"center": v(60.62, 74.09) * mm, "radius": 3.18 * mm});
            skCircle(sketch, "E11.0.17.15", {"center": v(60.62, 87.56) * mm, "radius": 3.18 * mm});
            skCircle(sketch, "E11.0.17.16", {"center": v(60.62, 101.03) * mm, "radius": 3.18 * mm});
            skCircle(sketch, "E11.0.17.17", {"center": v(60.62, 114.5) * mm, "radius": 3.18 * mm});
            skCircle(sketch, "E11.0.17.18", {"center": v(60.62, 127.97) * mm, "radius": 3.18 * mm});
            skCircle(sketch, "E11.0.17.19", {"center": v(60.62, 141.44) * mm, "radius": 3.18 * mm});
            skCircle(sketch, "E11.0.17.20", {"center": v(60.62, 154.9) * mm, "radius": 3.18 * mm});
            skCircle(sketch, "E11.0.17.21", {"center": v(60.62, 168.38) * mm, "radius": 3.18 * mm});
            skCircle(sketch, "E11.0.17.22", {"center": v(60.62, 181.85) * mm, "radius": 3.18 * mm});
            skCircle(sketch, "E11.0.17.23", {"center": v(60.62, 195.32) * mm, "radius": 3.18 * mm});
            skCircle(sketch, "E11.0.17.24", {"center": v(60.62, 208.8) * mm, "radius": 3.18 * mm});
            skCircle(sketch, "E11.0.18.0", {"center": v(74.09, -114.5) * mm, "radius": 3.18 * mm});
            skCircle(sketch, "E11.0.18.1", {"center": v(74.09, -101.03) * mm, "radius": 3.18 * mm});
            skCircle(sketch, "E11.0.18.2", {"center": v(74.09, -87.56) * mm, "radius": 3.18 * mm});
            skCircle(sketch, "E11.0.18.3", {"center": v(74.09, -74.09) * mm, "radius": 3.18 * mm});
            skCircle(sketch, "E11.0.18.4", {"center": v(74.09, -60.62) * mm, "radius": 3.18 * mm});
            skCircle(sketch, "E11.0.18.5", {"center": v(74.09, -47.15) * mm, "radius": 3.18 * mm});
            skCircle(sketch, "E11.0.18.6", {"center": v(74.09, -33.68) * mm, "radius": 3.18 * mm});
            skCircle(sketch, "E11.0.18.7", {"center": v(74.09, -20.2) * mm, "radius": 3.18 * mm});
            skCircle(sketch, "E11.0.18.8", {"center": v(74.09, -6.74) * mm, "radius": 3.18 * mm});
            skCircle(sketch, "E11.0.18.9", {"center": v(74.09, 6.74) * mm, "radius": 3.18 * mm});
            skCircle(sketch, "E11.0.18.10", {"center": v(74.09, 20.2) * mm, "radius": 3.18 * mm});
            skCircle(sketch, "E11.0.18.11", {"center": v(74.09, 33.68) * mm, "radius": 3.18 * mm});
            skCircle(sketch, "E11.0.18.12", {"center": v(74.09, 47.15) * mm, "radius": 3.18 * mm});
            skCircle(sketch, "E11.0.18.13", {"center": v(74.09, 60.62) * mm, "radius": 3.18 * mm});
            skCircle(sketch, "E11.0.18.14", {"center": v(74.09, 74.09) * mm, "radius": 3.18 * mm});
            skCircle(sketch, "E11.0.18.15", {"center": v(74.09, 87.56) * mm, "radius": 3.18 * mm});
            skCircle(sketch, "E11.0.18.16", {"center": v(74.09, 101.03) * mm, "radius": 3.18 * mm});
            skCircle(sketch, "E11.0.18.17", {"center": v(74.09, 114.5) * mm, "radius": 3.18 * mm});
            skCircle(sketch, "E11.0.18.18", {"center": v(74.09, 127.97) * mm, "radius": 3.18 * mm});
            skCircle(sketch, "E11.0.18.19", {"center": v(74.09, 141.44) * mm, "radius": 3.18 * mm});
            skCircle(sketch, "E11.0.18.20", {"center": v(74.09, 154.9) * mm, "radius": 3.18 * mm});
            skCircle(sketch, "E11.0.18.21", {"center": v(74.09, 168.38) * mm, "radius": 3.18 * mm});
            skCircle(sketch, "E11.0.18.22", {"center": v(74.09, 181.85) * mm, "radius": 3.18 * mm});
            skCircle(sketch, "E11.0.18.23", {"center": v(74.09, 195.32) * mm, "radius": 3.18 * mm});
            skCircle(sketch, "E11.0.18.24", {"center": v(74.09, 208.8) * mm, "radius": 3.18 * mm});
            skCircle(sketch, "E11.0.19.0", {"center": v(87.56, -114.5) * mm, "radius": 3.18 * mm});
            skCircle(sketch, "E11.0.19.1", {"center": v(87.56, -101.03) * mm, "radius": 3.18 * mm});
            skCircle(sketch, "E11.0.19.2", {"center": v(87.56, -87.56) * mm, "radius": 3.18 * mm});
            skCircle(sketch, "E11.0.19.3", {"center": v(87.56, -74.09) * mm, "radius": 3.18 * mm});
            skCircle(sketch, "E11.0.19.4", {"center": v(87.56, -60.62) * mm, "radius": 3.18 * mm});
            skCircle(sketch, "E11.0.19.5", {"center": v(87.56, -47.15) * mm, "radius": 3.18 * mm});
            skCircle(sketch, "E11.0.19.6", {"center": v(87.56, -33.68) * mm, "radius": 3.18 * mm});
            skCircle(sketch, "E11.0.19.7", {"center": v(87.56, -20.2) * mm, "radius": 3.18 * mm});
            skCircle(sketch, "E11.0.19.8", {"center": v(87.56, -6.74) * mm, "radius": 3.18 * mm});
            skCircle(sketch, "E11.0.19.9", {"center": v(87.56, 6.74) * mm, "radius": 3.18 * mm});
            skCircle(sketch, "E11.0.19.10", {"center": v(87.56, 20.2) * mm, "radius": 3.18 * mm});
            skCircle(sketch, "E11.0.19.11", {"center": v(87.56, 33.68) * mm, "radius": 3.18 * mm});
            skCircle(sketch, "E11.0.19.12", {"center": v(87.56, 47.15) * mm, "radius": 3.18 * mm});
            skCircle(sketch, "E11.0.19.13", {"center": v(87.56, 60.62) * mm, "radius": 3.18 * mm});
            skCircle(sketch, "E11.0.19.14", {"center": v(87.56, 74.09) * mm, "radius": 3.18 * mm});
            skCircle(sketch, "E11.0.19.15", {"center": v(87.56, 87.56) * mm, "radius": 3.18 * mm});
            skCircle(sketch, "E11.0.19.16", {"center": v(87.56, 101.03) * mm, "radius": 3.18 * mm});
            skCircle(sketch, "E11.0.19.17", {"center": v(87.56, 114.5) * mm, "radius": 3.18 * mm});
            skCircle(sketch, "E11.0.19.18", {"center": v(87.56, 127.97) * mm, "radius": 3.18 * mm});
            skCircle(sketch, "E11.0.19.19", {"center": v(87.56, 141.44) * mm, "radius": 3.18 * mm});
            skCircle(sketch, "E11.0.19.20", {"center": v(87.56, 154.9) * mm, "radius": 3.18 * mm});
            skCircle(sketch, "E11.0.19.21", {"center": v(87.56, 168.38) * mm, "radius": 3.18 * mm});
            skCircle(sketch, "E11.0.19.22", {"center": v(87.56, 181.85) * mm, "radius": 3.18 * mm});
            skCircle(sketch, "E11.0.19.23", {"center": v(87.56, 195.32) * mm, "radius": 3.18 * mm});
            skCircle(sketch, "E11.0.19.24", {"center": v(87.56, 208.8) * mm, "radius": 3.18 * mm});
            skCircle(sketch, "E11.0.20.0", {"center": v(101.03, -114.5) * mm, "radius": 3.18 * mm});
            skCircle(sketch, "E11.0.20.1", {"center": v(101.03, -101.03) * mm, "radius": 3.18 * mm});
            skCircle(sketch, "E11.0.20.2", {"center": v(101.03, -87.56) * mm, "radius": 3.18 * mm});
            skCircle(sketch, "E11.0.20.3", {"center": v(101.03, -74.09) * mm, "radius": 3.18 * mm});
            skCircle(sketch, "E11.0.20.4", {"center": v(101.03, -60.62) * mm, "radius": 3.18 * mm});
            skCircle(sketch, "E11.0.20.5", {"center": v(101.03, -47.15) * mm, "radius": 3.18 * mm});
            skCircle(sketch, "E11.0.20.6", {"center": v(101.03, -33.68) * mm, "radius": 3.18 * mm});
            skCircle(sketch, "E11.0.20.7", {"center": v(101.03, -20.2) * mm, "radius": 3.18 * mm});
            skCircle(sketch, "E11.0.20.8", {"center": v(101.03, -6.74) * mm, "radius": 3.18 * mm});
            skCircle(sketch, "E11.0.20.9", {"center": v(101.03, 6.74) * mm, "radius": 3.18 * mm});
            skCircle(sketch, "E11.0.20.10", {"center": v(101.03, 20.2) * mm, "radius": 3.18 * mm});
            skCircle(sketch, "E11.0.20.11", {"center": v(101.03, 33.68) * mm, "radius": 3.18 * mm});
            skCircle(sketch, "E11.0.20.12", {"center": v(101.03, 47.15) * mm, "radius": 3.18 * mm});
            skCircle(sketch, "E11.0.20.13", {"center": v(101.03, 60.62) * mm, "radius": 3.18 * mm});
            skCircle(sketch, "E11.0.20.14", {"center": v(101.03, 74.09) * mm, "radius": 3.18 * mm});
            skCircle(sketch, "E11.0.20.15", {"center": v(101.03, 87.56) * mm, "radius": 3.18 * mm});
            skCircle(sketch, "E11.0.20.16", {"center": v(101.03, 101.03) * mm, "radius": 3.18 * mm});
            skCircle(sketch, "E11.0.20.17", {"center": v(101.03, 114.5) * mm, "radius": 3.18 * mm});
            skCircle(sketch, "E11.0.20.18", {"center": v(101.03, 127.97) * mm, "radius": 3.18 * mm});
            skCircle(sketch, "E11.0.20.19", {"center": v(101.03, 141.44) * mm, "radius": 3.18 * mm});
            skCircle(sketch, "E11.0.20.20", {"center": v(101.03, 154.9) * mm, "radius": 3.18 * mm});
            skCircle(sketch, "E11.0.20.21", {"center": v(101.03, 168.38) * mm, "radius": 3.18 * mm});
            skCircle(sketch, "E11.0.20.22", {"center": v(101.03, 181.85) * mm, "radius": 3.18 * mm});
            skCircle(sketch, "E11.0.20.23", {"center": v(101.03, 195.32) * mm, "radius": 3.18 * mm});
            skCircle(sketch, "E11.0.20.24", {"center": v(101.03, 208.8) * mm, "radius": 3.18 * mm});
            skCircle(sketch, "E11.0.21.0", {"center": v(114.5, -114.5) * mm, "radius": 3.18 * mm});
            skCircle(sketch, "E11.0.21.1", {"center": v(114.5, -101.03) * mm, "radius": 3.18 * mm});
            skCircle(sketch, "E11.0.21.2", {"center": v(114.5, -87.56) * mm, "radius": 3.18 * mm});
            skCircle(sketch, "E11.0.21.3", {"center": v(114.5, -74.09) * mm, "radius": 3.18 * mm});
            skCircle(sketch, "E11.0.21.4", {"center": v(114.5, -60.62) * mm, "radius": 3.18 * mm});
            skCircle(sketch, "E11.0.21.5", {"center": v(114.5, -47.15) * mm, "radius": 3.18 * mm});
            skCircle(sketch, "E11.0.21.6", {"center": v(114.5, -33.68) * mm, "radius": 3.18 * mm});
            skCircle(sketch, "E11.0.21.7", {"center": v(114.5, -20.2) * mm, "radius": 3.18 * mm});
            skCircle(sketch, "E11.0.21.8", {"center": v(114.5, -6.74) * mm, "radius": 3.18 * mm});
            skCircle(sketch, "E11.0.21.9", {"center": v(114.5, 6.74) * mm, "radius": 3.18 * mm});
            skCircle(sketch, "E11.0.21.10", {"center": v(114.5, 20.2) * mm, "radius": 3.18 * mm});
            skCircle(sketch, "E11.0.21.11", {"center": v(114.5, 33.68) * mm, "radius": 3.18 * mm});
            skCircle(sketch, "E11.0.21.12", {"center": v(114.5, 47.15) * mm, "radius": 3.18 * mm});
            skCircle(sketch, "E11.0.21.13", {"center": v(114.5, 60.62) * mm, "radius": 3.18 * mm});
            skCircle(sketch, "E11.0.21.14", {"center": v(114.5, 74.09) * mm, "radius": 3.18 * mm});
            skCircle(sketch, "E11.0.21.15", {"center": v(114.5, 87.56) * mm, "radius": 3.18 * mm});
            skCircle(sketch, "E11.0.21.16", {"center": v(114.5, 101.03) * mm, "radius": 3.18 * mm});
            skCircle(sketch, "E11.0.21.17", {"center": v(114.5, 114.5) * mm, "radius": 3.18 * mm});
            skCircle(sketch, "E11.0.21.18", {"center": v(114.5, 127.97) * mm, "radius": 3.18 * mm});
            skCircle(sketch, "E11.0.21.19", {"center": v(114.5, 141.44) * mm, "radius": 3.18 * mm});
            skCircle(sketch, "E11.0.21.20", {"center": v(114.5, 154.9) * mm, "radius": 3.18 * mm});
            skCircle(sketch, "E11.0.21.21", {"center": v(114.5, 168.38) * mm, "radius": 3.18 * mm});
            skCircle(sketch, "E11.0.21.22", {"center": v(114.5, 181.85) * mm, "radius": 3.18 * mm});
            skCircle(sketch, "E11.0.21.23", {"center": v(114.5, 195.32) * mm, "radius": 3.18 * mm});
            skCircle(sketch, "E11.0.21.24", {"center": v(114.5, 208.8) * mm, "radius": 3.18 * mm});
            skCircle(sketch, "E11.0.22.0", {"center": v(127.97, -114.5) * mm, "radius": 3.18 * mm});
            skCircle(sketch, "E11.0.22.1", {"center": v(127.97, -101.03) * mm, "radius": 3.18 * mm});
            skCircle(sketch, "E11.0.22.2", {"center": v(127.97, -87.56) * mm, "radius": 3.18 * mm});
            skCircle(sketch, "E11.0.22.3", {"center": v(127.97, -74.09) * mm, "radius": 3.18 * mm});
            skCircle(sketch, "E11.0.22.4", {"center": v(127.97, -60.62) * mm, "radius": 3.18 * mm});
            skCircle(sketch, "E11.0.22.5", {"center": v(127.97, -47.15) * mm, "radius": 3.18 * mm});
            skCircle(sketch, "E11.0.22.6", {"center": v(127.97, -33.68) * mm, "radius": 3.18 * mm});
            skCircle(sketch, "E11.0.22.7", {"center": v(127.97, -20.2) * mm, "radius": 3.18 * mm});
            skCircle(sketch, "E11.0.22.8", {"center": v(127.97, -6.74) * mm, "radius": 3.18 * mm});
            skCircle(sketch, "E11.0.22.9", {"center": v(127.97, 6.74) * mm, "radius": 3.18 * mm});
            skCircle(sketch, "E11.0.22.10", {"center": v(127.97, 20.2) * mm, "radius": 3.18 * mm});
            skCircle(sketch, "E11.0.22.11", {"center": v(127.97, 33.68) * mm, "radius": 3.18 * mm});
            skCircle(sketch, "E11.0.22.12", {"center": v(127.97, 47.15) * mm, "radius": 3.18 * mm});
            skCircle(sketch, "E11.0.22.13", {"center": v(127.97, 60.62) * mm, "radius": 3.18 * mm});
            skCircle(sketch, "E11.0.22.14", {"center": v(127.97, 74.09) * mm, "radius": 3.18 * mm});
            skCircle(sketch, "E11.0.22.15", {"center": v(127.97, 87.56) * mm, "radius": 3.18 * mm});
            skCircle(sketch, "E11.0.22.16", {"center": v(127.97, 101.03) * mm, "radius": 3.18 * mm});
            skCircle(sketch, "E11.0.22.17", {"center": v(127.97, 114.5) * mm, "radius": 3.18 * mm});
            skCircle(sketch, "E11.0.22.18", {"center": v(127.97, 127.97) * mm, "radius": 3.18 * mm});
            skCircle(sketch, "E11.0.22.19", {"center": v(127.97, 141.44) * mm, "radius": 3.18 * mm});
            skCircle(sketch, "E11.0.22.20", {"center": v(127.97, 154.9) * mm, "radius": 3.18 * mm});
            skCircle(sketch, "E11.0.22.21", {"center": v(127.97, 168.38) * mm, "radius": 3.18 * mm});
            skCircle(sketch, "E11.0.22.22", {"center": v(127.97, 181.85) * mm, "radius": 3.18 * mm});
            skCircle(sketch, "E11.0.22.23", {"center": v(127.97, 195.32) * mm, "radius": 3.18 * mm});
            skCircle(sketch, "E11.0.22.24", {"center": v(127.97, 208.8) * mm, "radius": 3.18 * mm});
            skCircle(sketch, "E11.0.23.0", {"center": v(141.44, -114.5) * mm, "radius": 3.18 * mm});
            skCircle(sketch, "E11.0.23.1", {"center": v(141.44, -101.03) * mm, "radius": 3.18 * mm});
            skCircle(sketch, "E11.0.23.2", {"center": v(141.44, -87.56) * mm, "radius": 3.18 * mm});
            skCircle(sketch, "E11.0.23.3", {"center": v(141.44, -74.09) * mm, "radius": 3.18 * mm});
            skCircle(sketch, "E11.0.23.4", {"center": v(141.44, -60.62) * mm, "radius": 3.18 * mm});
            skCircle(sketch, "E11.0.23.5", {"center": v(141.44, -47.15) * mm, "radius": 3.18 * mm});
            skCircle(sketch, "E11.0.23.6", {"center": v(141.44, -33.68) * mm, "radius": 3.18 * mm});
            skCircle(sketch, "E11.0.23.7", {"center": v(141.44, -20.2) * mm, "radius": 3.18 * mm});
            skCircle(sketch, "E11.0.23.8", {"center": v(141.44, -6.74) * mm, "radius": 3.18 * mm});
            skCircle(sketch, "E11.0.23.9", {"center": v(141.44, 6.74) * mm, "radius": 3.18 * mm});
            skCircle(sketch, "E11.0.23.10", {"center": v(141.44, 20.2) * mm, "radius": 3.18 * mm});
            skCircle(sketch, "E11.0.23.11", {"center": v(141.44, 33.68) * mm, "radius": 3.18 * mm});
            skCircle(sketch, "E11.0.23.12", {"center": v(141.44, 47.15) * mm, "radius": 3.18 * mm});
            skCircle(sketch, "E11.0.23.13", {"center": v(141.44, 60.62) * mm, "radius": 3.18 * mm});
            skCircle(sketch, "E11.0.23.14", {"center": v(141.44, 74.09) * mm, "radius": 3.18 * mm});
            skCircle(sketch, "E11.0.23.15", {"center": v(141.44, 87.56) * mm, "radius": 3.18 * mm});
            skCircle(sketch, "E11.0.23.16", {"center": v(141.44, 101.03) * mm, "radius": 3.18 * mm});
            skCircle(sketch, "E11.0.23.17", {"center": v(141.44, 114.5) * mm, "radius": 3.18 * mm});
            skCircle(sketch, "E11.0.23.18", {"center": v(141.44, 127.97) * mm, "radius": 3.18 * mm});
            skCircle(sketch, "E11.0.23.19", {"center": v(141.44, 141.44) * mm, "radius": 3.18 * mm});
            skCircle(sketch, "E11.0.23.20", {"center": v(141.44, 154.9) * mm, "radius": 3.18 * mm});
            skCircle(sketch, "E11.0.23.21", {"center": v(141.44, 168.38) * mm, "radius": 3.18 * mm});
            skCircle(sketch, "E11.0.23.22", {"center": v(141.44, 181.85) * mm, "radius": 3.18 * mm});
            skCircle(sketch, "E11.0.23.23", {"center": v(141.44, 195.32) * mm, "radius": 3.18 * mm});
            skCircle(sketch, "E11.0.23.24", {"center": v(141.44, 208.8) * mm, "radius": 3.18 * mm});
            skCircle(sketch, "E11.0.24.0", {"center": v(154.9, -114.5) * mm, "radius": 3.18 * mm});
            skCircle(sketch, "E11.0.24.1", {"center": v(154.9, -101.03) * mm, "radius": 3.18 * mm});
            skCircle(sketch, "E11.0.24.2", {"center": v(154.9, -87.56) * mm, "radius": 3.18 * mm});
            skCircle(sketch, "E11.0.24.3", {"center": v(154.9, -74.09) * mm, "radius": 3.18 * mm});
            skCircle(sketch, "E11.0.24.4", {"center": v(154.9, -60.62) * mm, "radius": 3.18 * mm});
            skCircle(sketch, "E11.0.24.5", {"center": v(154.9, -47.15) * mm, "radius": 3.18 * mm});
            skCircle(sketch, "E11.0.24.6", {"center": v(154.9, -33.68) * mm, "radius": 3.18 * mm});
            skCircle(sketch, "E11.0.24.7", {"center": v(154.9, -20.2) * mm, "radius": 3.18 * mm});
            skCircle(sketch, "E11.0.24.8", {"center": v(154.9, -6.74) * mm, "radius": 3.18 * mm});
            skCircle(sketch, "E11.0.24.9", {"center": v(154.9, 6.74) * mm, "radius": 3.18 * mm});
            skCircle(sketch, "E11.0.24.10", {"center": v(154.9, 20.2) * mm, "radius": 3.18 * mm});
            skCircle(sketch, "E11.0.24.11", {"center": v(154.9, 33.68) * mm, "radius": 3.18 * mm});
            skCircle(sketch, "E11.0.24.12", {"center": v(154.9, 47.15) * mm, "radius": 3.18 * mm});
            skCircle(sketch, "E11.0.24.13", {"center": v(154.9, 60.62) * mm, "radius": 3.18 * mm});
            skCircle(sketch, "E11.0.24.14", {"center": v(154.9, 74.09) * mm, "radius": 3.18 * mm});
            skCircle(sketch, "E11.0.24.15", {"center": v(154.9, 87.56) * mm, "radius": 3.18 * mm});
            skCircle(sketch, "E11.0.24.16", {"center": v(154.9, 101.03) * mm, "radius": 3.18 * mm});
            skCircle(sketch, "E11.0.24.17", {"center": v(154.9, 114.5) * mm, "radius": 3.18 * mm});
            skCircle(sketch, "E11.0.24.18", {"center": v(154.9, 127.97) * mm, "radius": 3.18 * mm});
            skCircle(sketch, "E11.0.24.19", {"center": v(154.9, 141.44) * mm, "radius": 3.18 * mm});
            skCircle(sketch, "E11.0.24.20", {"center": v(154.9, 154.9) * mm, "radius": 3.18 * mm});
            skCircle(sketch, "E11.0.24.21", {"center": v(154.9, 168.38) * mm, "radius": 3.18 * mm});
            skCircle(sketch, "E11.0.24.22", {"center": v(154.9, 181.85) * mm, "radius": 3.18 * mm});
            skCircle(sketch, "E11.0.24.23", {"center": v(154.9, 195.32) * mm, "radius": 3.18 * mm});
            skCircle(sketch, "E11.0.24.24", {"center": v(154.9, 208.8) * mm, "radius": 3.18 * mm});
            skSolve(sketch);
        }
        {
            var Q0;
            Q0 = qSketchRegion(id + "F2", true);
            extrude(context, id + "F3", {"entities" : qUnion([Q0]), "operationType" : NewBodyOperationType.REMOVE, "oppositeDirection" : true, "depth" : 25.4 * mm, "offsetDistance" : 25.4 * mm});
        }
        {
            var Q0;
            Q0=makeQuery(id+"F1.opExtrude","CAP_FACE",FACE,{"disambiguationData":[OSD([sQuery(id+"F0.wireOp",EDGE,"E0")])],"isStart":false});
            var sketch = newSketch(context, id + "F4", { "sketchPlane" : qUnion([Q0])});
            skCircle(sketch, "E12", {"center": v(0, 0) * mm, "radius": 123.02 * mm});
            skCircle(sketch, "E13", {"center": v(0, 0) * mm, "radius": 115.89 * mm});
            skSolve(sketch);
        }
        {
            var Q0;
            Q0 = qSketchRegion(id + "F4", true);
            var Q1;
            Q1=makeQuery(id+"F1.opExtrude","CAP_FACE",FACE,{"disambiguationData":[OSD([sQuery(id+"F0.wireOp",EDGE,"E0")])],"isStart":true});
            extrude(context, id + "F5", {"entities" : qUnion([Q0]), "operationType" : NewBodyOperationType.ADD, "endBound" : BoundingType.UP_TO_SURFACE, "oppositeDirection" : true, "depth" : 25.4 * mm, "endBoundEntityFace" : qUnion([Q1]), "offsetDistance" : 25.4 * mm});
        }
    });
